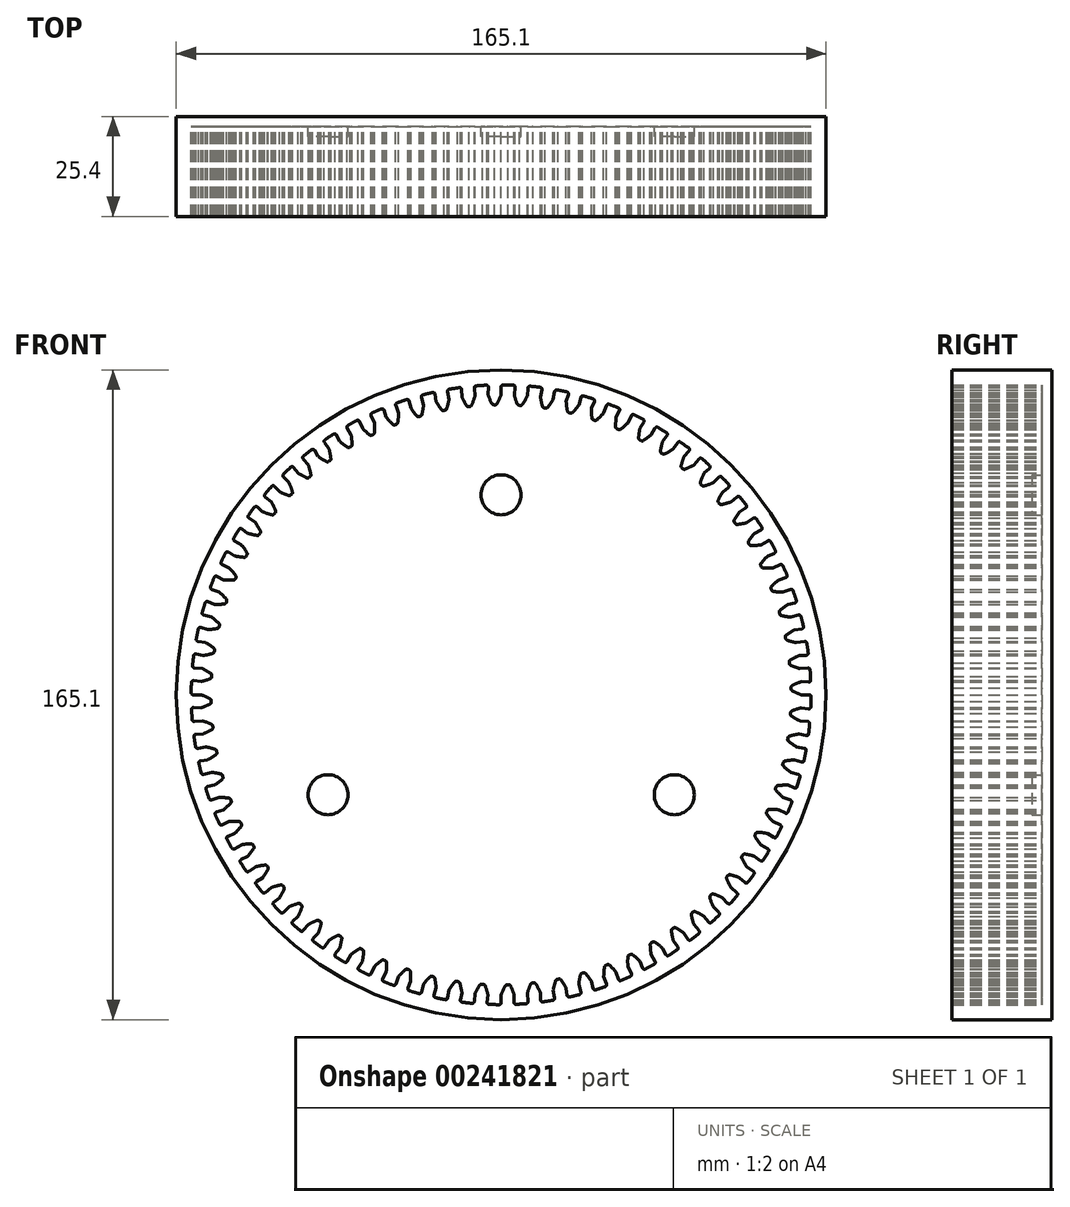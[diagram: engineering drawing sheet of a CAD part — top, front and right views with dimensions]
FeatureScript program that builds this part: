
annotation { "Feature Type Name" : "Feature", "Feature Type Description" : "" }
export const myFeature = defineFeature(function(context is Context, id is Id, definition is map)
    precondition{}
    {
        {
            var Q0;
            Q0=qCreatedBy(makeId("Front.planeOp"),FACE);
            var sketch = newSketch(context, id + "F0", { "sketchPlane" : qUnion([Q0])});
            skArc(sketch, "E0", {"start": v(-3.78, 78.65) * mm, "mid": v(-5.06, 78.58) * mm, "end": v(-6.35, 78.48) * mm});
            skLineSegment(sketch, "E1.MirrorCS", {"start": v(-1.94, 73.68) * mm, "end": v(-1.72, 73.67) * mm});
            skLineSegment(sketch, "E2.MirrorCS", {"start": v(-1.5, 73.67) * mm, "end": v(-1.72, 73.67) * mm});
            skArc(sketch, "E3.MirrorCS", {"start": v(0, 76.2) * mm, "mid": v(-0.49, 75.05) * mm, "end": v(-1.05, 73.93) * mm});
            skArc(sketch, "E4.MirrorCS", {"start": v(-3.32, 76.27) * mm, "mid": v(-2.89, 75.1) * mm, "end": v(-2.38, 73.96) * mm});
            skLineSegment(sketch, "E5.MirrorCS", {"start": v(-3.32, 76.27) * mm, "end": v(-3.24, 78.12) * mm});
            skLineSegment(sketch, "E6.MirrorCS", {"start": v(0, 76.2) * mm, "end": v(0, 78.23) * mm});
            skPoint(sketch, "E7.visualSharp", {"position": v(-1.2, 73.67) * mm});
            skArc(sketch, "E7.filletArc", {"start": v(-1.5, 73.67) * mm, "mid": v(-1.23, 73.74) * mm, "end": v(-1.05, 73.93) * mm});
            skPoint(sketch, "E8.visualSharp", {"position": v(0, 78.74) * mm});
            skArc(sketch, "E8.filletArc", {"start": v(0.51, 78.74) * mm, "mid": v(0.15, 78.6) * mm, "end": v(0, 78.23) * mm});
            skPoint(sketch, "E9.visualSharp", {"position": v(-3.22, 78.67) * mm});
            skArc(sketch, "E9.filletArc", {"start": v(-3.24, 78.12) * mm, "mid": v(-3.4, 78.5) * mm, "end": v(-3.78, 78.65) * mm});
            skPoint(sketch, "E10.visualSharp", {"position": v(-2.24, 73.7) * mm});
            skArc(sketch, "E10.filletArc", {"start": v(-2.38, 73.96) * mm, "mid": v(-2.2, 73.76) * mm, "end": v(-1.94, 73.68) * mm});
            skArc(sketch, "E11.1.0", {"start": v(-6.35, 78.48) * mm, "mid": v(-6.7, 78.3) * mm, "end": v(-6.82, 77.93) * mm});
            skLineSegment(sketch, "E11.1.1", {"start": v(-6.64, 75.91) * mm, "end": v(-6.82, 77.93) * mm});
            skArc(sketch, "E11.1.2", {"start": v(-6.64, 75.91) * mm, "mid": v(-7.03, 74.72) * mm, "end": v(-7.49, 73.56) * mm});
            skArc(sketch, "E11.1.3", {"start": v(-7.9, 73.26) * mm, "mid": v(-7.66, 73.35) * mm, "end": v(-7.49, 73.56) * mm});
            skLineSegment(sketch, "E11.1.4", {"start": v(-7.9, 73.26) * mm, "end": v(-8.13, 73.24) * mm});
            skLineSegment(sketch, "E11.1.5", {"start": v(-8.36, 73.23) * mm, "end": v(-8.13, 73.24) * mm});
            skArc(sketch, "E11.1.6", {"start": v(-8.81, 73.47) * mm, "mid": v(-8.62, 73.29) * mm, "end": v(-8.36, 73.23) * mm});
            skArc(sketch, "E11.1.7", {"start": v(-9.96, 75.7) * mm, "mid": v(-9.42, 74.56) * mm, "end": v(-8.81, 73.47) * mm});
            skLineSegment(sketch, "E11.1.8", {"start": v(-9.96, 75.7) * mm, "end": v(-10.04, 77.54) * mm});
            skArc(sketch, "E11.1.9", {"start": v(-10.04, 77.54) * mm, "mid": v(-10.22, 77.9) * mm, "end": v(-10.62, 78.02) * mm});
            skArc(sketch, "E11.2.0", {"start": v(-13.17, 77.63) * mm, "mid": v(-13.5, 77.42) * mm, "end": v(-13.58, 77.04) * mm});
            skLineSegment(sketch, "E11.2.1", {"start": v(-13.23, 75.04) * mm, "end": v(-13.58, 77.04) * mm});
            skArc(sketch, "E11.2.2", {"start": v(-13.23, 75.04) * mm, "mid": v(-13.51, 73.83) * mm, "end": v(-13.87, 72.63) * mm});
            skArc(sketch, "E11.2.3", {"start": v(-14.26, 72.3) * mm, "mid": v(-14.02, 72.4) * mm, "end": v(-13.87, 72.63) * mm});
            skLineSegment(sketch, "E11.2.4", {"start": v(-14.26, 72.3) * mm, "end": v(-14.48, 72.25) * mm});
            skLineSegment(sketch, "E11.2.5", {"start": v(-14.7, 72.22) * mm, "end": v(-14.48, 72.25) * mm});
            skArc(sketch, "E11.2.6", {"start": v(-15.18, 72.43) * mm, "mid": v(-14.97, 72.26) * mm, "end": v(-14.7, 72.22) * mm});
            skArc(sketch, "E11.2.7", {"start": v(-16.52, 74.54) * mm, "mid": v(-15.89, 73.46) * mm, "end": v(-15.18, 72.43) * mm});
            skLineSegment(sketch, "E11.2.8", {"start": v(-16.52, 74.54) * mm, "end": v(-16.76, 76.37) * mm});
            skArc(sketch, "E11.2.9", {"start": v(-16.76, 76.37) * mm, "mid": v(-16.97, 76.72) * mm, "end": v(-17.37, 76.8) * mm});
            skArc(sketch, "E11.3.0", {"start": v(-19.89, 76.19) * mm, "mid": v(-20.2, 75.95) * mm, "end": v(-20.25, 75.56) * mm});
            skLineSegment(sketch, "E11.3.1", {"start": v(-19.72, 73.6) * mm, "end": v(-20.25, 75.56) * mm});
            skArc(sketch, "E11.3.2", {"start": v(-19.72, 73.6) * mm, "mid": v(-19.9, 72.37) * mm, "end": v(-20.15, 71.14) * mm});
            skArc(sketch, "E11.3.3", {"start": v(-20.5, 70.77) * mm, "mid": v(-20.28, 70.9) * mm, "end": v(-20.15, 71.14) * mm});
            skLineSegment(sketch, "E11.3.4", {"start": v(-20.5, 70.77) * mm, "end": v(-20.73, 70.71) * mm});
            skLineSegment(sketch, "E11.3.5", {"start": v(-20.95, 70.67) * mm, "end": v(-20.73, 70.71) * mm});
            skArc(sketch, "E11.3.6", {"start": v(-21.44, 70.83) * mm, "mid": v(-21.21, 70.68) * mm, "end": v(-20.95, 70.67) * mm});
            skArc(sketch, "E11.3.7", {"start": v(-22.95, 72.81) * mm, "mid": v(-22.23, 71.8) * mm, "end": v(-21.44, 70.83) * mm});
            skLineSegment(sketch, "E11.3.8", {"start": v(-22.95, 72.81) * mm, "end": v(-23.35, 74.62) * mm});
            skArc(sketch, "E11.3.9", {"start": v(-23.35, 74.62) * mm, "mid": v(-23.6, 74.95) * mm, "end": v(-24, 75) * mm});
            skArc(sketch, "E11.4.0", {"start": v(-26.45, 74.16) * mm, "mid": v(-26.74, 73.9) * mm, "end": v(-26.76, 73.51) * mm});
            skLineSegment(sketch, "E11.4.1", {"start": v(-26.06, 71.6) * mm, "end": v(-26.76, 73.51) * mm});
            skArc(sketch, "E11.4.2", {"start": v(-26.06, 71.6) * mm, "mid": v(-26.13, 70.36) * mm, "end": v(-26.27, 69.12) * mm});
            skArc(sketch, "E11.4.3", {"start": v(-26.6, 68.72) * mm, "mid": v(-26.38, 68.87) * mm, "end": v(-26.27, 69.12) * mm});
            skLineSegment(sketch, "E11.4.4", {"start": v(-26.6, 68.72) * mm, "end": v(-26.81, 68.64) * mm});
            skLineSegment(sketch, "E11.4.5", {"start": v(-27.03, 68.57) * mm, "end": v(-26.81, 68.64) * mm});
            skArc(sketch, "E11.4.6", {"start": v(-27.53, 68.69) * mm, "mid": v(-27.3, 68.56) * mm, "end": v(-27.03, 68.57) * mm});
            skArc(sketch, "E11.4.7", {"start": v(-29.21, 70.54) * mm, "mid": v(-28.4, 69.59) * mm, "end": v(-27.53, 68.69) * mm});
            skLineSegment(sketch, "E11.4.8", {"start": v(-29.21, 70.54) * mm, "end": v(-29.77, 72.3) * mm});
            skArc(sketch, "E11.4.9", {"start": v(-29.77, 72.3) * mm, "mid": v(-30.04, 72.6) * mm, "end": v(-30.45, 72.62) * mm});
            skArc(sketch, "E11.5.0", {"start": v(-32.81, 71.58) * mm, "mid": v(-33.08, 71.3) * mm, "end": v(-33.06, 70.9) * mm});
            skLineSegment(sketch, "E11.5.1", {"start": v(-32.2, 69.06) * mm, "end": v(-33.06, 70.9) * mm});
            skArc(sketch, "E11.5.2", {"start": v(-32.2, 69.06) * mm, "mid": v(-32.16, 67.81) * mm, "end": v(-32.2, 66.56) * mm});
            skArc(sketch, "E11.5.3", {"start": v(-32.49, 66.14) * mm, "mid": v(-32.28, 66.31) * mm, "end": v(-32.2, 66.56) * mm});
            skLineSegment(sketch, "E11.5.4", {"start": v(-32.49, 66.14) * mm, "end": v(-32.7, 66.04) * mm});
            skLineSegment(sketch, "E11.5.5", {"start": v(-32.9, 65.95) * mm, "end": v(-32.7, 66.04) * mm});
            skArc(sketch, "E11.5.6", {"start": v(-33.41, 66.03) * mm, "mid": v(-33.17, 65.92) * mm, "end": v(-32.9, 65.95) * mm});
            skArc(sketch, "E11.5.7", {"start": v(-35.25, 67.72) * mm, "mid": v(-34.36, 66.85) * mm, "end": v(-33.41, 66.03) * mm});
            skLineSegment(sketch, "E11.5.8", {"start": v(-35.25, 67.72) * mm, "end": v(-35.95, 69.43) * mm});
            skArc(sketch, "E11.5.9", {"start": v(-35.95, 69.43) * mm, "mid": v(-36.25, 69.71) * mm, "end": v(-36.66, 69.69) * mm});
            skArc(sketch, "E11.6.0", {"start": v(-38.93, 68.45) * mm, "mid": v(-39.17, 68.14) * mm, "end": v(-39.12, 67.75) * mm});
            skLineSegment(sketch, "E11.6.1", {"start": v(-38.1, 66) * mm, "end": v(-39.12, 67.75) * mm});
            skArc(sketch, "E11.6.2", {"start": v(-38.1, 66) * mm, "mid": v(-37.95, 64.75) * mm, "end": v(-37.87, 63.5) * mm});
            skArc(sketch, "E11.6.3", {"start": v(-38.13, 63.05) * mm, "mid": v(-37.94, 63.24) * mm, "end": v(-37.87, 63.5) * mm});
            skLineSegment(sketch, "E11.6.4", {"start": v(-38.13, 63.05) * mm, "end": v(-38.32, 62.94) * mm});
            skLineSegment(sketch, "E11.6.5", {"start": v(-38.52, 62.84) * mm, "end": v(-38.32, 62.94) * mm});
            skArc(sketch, "E11.6.6", {"start": v(-39.04, 62.87) * mm, "mid": v(-38.79, 62.78) * mm, "end": v(-38.52, 62.84) * mm});
            skArc(sketch, "E11.6.7", {"start": v(-41.01, 64.4) * mm, "mid": v(-40.05, 63.6) * mm, "end": v(-39.04, 62.87) * mm});
            skLineSegment(sketch, "E11.6.8", {"start": v(-41.01, 64.4) * mm, "end": v(-41.87, 66.03) * mm});
            skArc(sketch, "E11.6.9", {"start": v(-41.87, 66.03) * mm, "mid": v(-42.19, 66.29) * mm, "end": v(-42.6, 66.22) * mm});
            skArc(sketch, "E11.7.0", {"start": v(-44.74, 64.8) * mm, "mid": v(-44.95, 64.46) * mm, "end": v(-44.87, 64.08) * mm});
            skLineSegment(sketch, "E11.7.1", {"start": v(-43.7, 62.42) * mm, "end": v(-44.87, 64.08) * mm});
            skArc(sketch, "E11.7.2", {"start": v(-43.7, 62.42) * mm, "mid": v(-43.45, 61.2) * mm, "end": v(-43.26, 59.96) * mm});
            skArc(sketch, "E11.7.3", {"start": v(-43.48, 59.49) * mm, "mid": v(-43.3, 59.7) * mm, "end": v(-43.26, 59.96) * mm});
            skLineSegment(sketch, "E11.7.4", {"start": v(-43.48, 59.49) * mm, "end": v(-43.66, 59.36) * mm});
            skLineSegment(sketch, "E11.7.5", {"start": v(-43.85, 59.24) * mm, "end": v(-43.66, 59.36) * mm});
            skArc(sketch, "E11.7.6", {"start": v(-44.37, 59.22) * mm, "mid": v(-44.1, 59.16) * mm, "end": v(-43.85, 59.24) * mm});
            skArc(sketch, "E11.7.7", {"start": v(-46.47, 60.57) * mm, "mid": v(-45.44, 59.86) * mm, "end": v(-44.37, 59.22) * mm});
            skLineSegment(sketch, "E11.7.8", {"start": v(-46.47, 60.57) * mm, "end": v(-47.46, 62.13) * mm});
            skArc(sketch, "E11.7.9", {"start": v(-47.46, 62.13) * mm, "mid": v(-47.8, 62.36) * mm, "end": v(-48.2, 62.26) * mm});
            skArc(sketch, "E11.8.0", {"start": v(-50.22, 60.65) * mm, "mid": v(-50.4, 60.3) * mm, "end": v(-50.29, 59.93) * mm});
            skLineSegment(sketch, "E11.8.1", {"start": v(-48.98, 58.37) * mm, "end": v(-50.29, 59.93) * mm});
            skArc(sketch, "E11.8.2", {"start": v(-48.98, 58.37) * mm, "mid": v(-48.61, 57.18) * mm, "end": v(-48.33, 55.96) * mm});
            skArc(sketch, "E11.8.3", {"start": v(-48.5, 55.47) * mm, "mid": v(-48.34, 55.7) * mm, "end": v(-48.33, 55.96) * mm});
            skLineSegment(sketch, "E11.8.4", {"start": v(-48.5, 55.47) * mm, "end": v(-48.67, 55.33) * mm});
            skLineSegment(sketch, "E11.8.5", {"start": v(-48.85, 55.2) * mm, "end": v(-48.67, 55.33) * mm});
            skArc(sketch, "E11.8.6", {"start": v(-49.36, 55.13) * mm, "mid": v(-49.1, 55.1) * mm, "end": v(-48.85, 55.2) * mm});
            skArc(sketch, "E11.8.7", {"start": v(-51.57, 56.3) * mm, "mid": v(-50.49, 55.68) * mm, "end": v(-49.36, 55.13) * mm});
            skLineSegment(sketch, "E11.8.8", {"start": v(-51.57, 56.3) * mm, "end": v(-52.7, 57.76) * mm});
            skArc(sketch, "E11.8.9", {"start": v(-52.7, 57.76) * mm, "mid": v(-53.06, 57.96) * mm, "end": v(-53.45, 57.82) * mm});
            skArc(sketch, "E11.9.0", {"start": v(-55.31, 56.04) * mm, "mid": v(-55.47, 55.68) * mm, "end": v(-55.32, 55.32) * mm});
            skLineSegment(sketch, "E11.9.1", {"start": v(-53.88, 53.88) * mm, "end": v(-55.32, 55.32) * mm});
            skArc(sketch, "E11.9.2", {"start": v(-53.88, 53.88) * mm, "mid": v(-53.41, 52.72) * mm, "end": v(-53.02, 51.54) * mm});
            skArc(sketch, "E11.9.3", {"start": v(-53.15, 51.04) * mm, "mid": v(-53.01, 51.27) * mm, "end": v(-53.02, 51.54) * mm});
            skLineSegment(sketch, "E11.9.4", {"start": v(-53.15, 51.04) * mm, "end": v(-53.3, 50.88) * mm});
            skLineSegment(sketch, "E11.9.5", {"start": v(-53.47, 50.73) * mm, "end": v(-53.3, 50.88) * mm});
            skArc(sketch, "E11.9.6", {"start": v(-53.98, 50.62) * mm, "mid": v(-53.71, 50.6) * mm, "end": v(-53.47, 50.73) * mm});
            skArc(sketch, "E11.9.7", {"start": v(-56.28, 51.58) * mm, "mid": v(-55.15, 51.06) * mm, "end": v(-53.98, 50.62) * mm});
            skLineSegment(sketch, "E11.9.8", {"start": v(-56.28, 51.58) * mm, "end": v(-57.53, 52.95) * mm});
            skArc(sketch, "E11.9.9", {"start": v(-57.53, 52.95) * mm, "mid": v(-57.9, 53.11) * mm, "end": v(-58.28, 52.94) * mm});
            skArc(sketch, "E11.10.0", {"start": v(-59.99, 51) * mm, "mid": v(-60.1, 50.63) * mm, "end": v(-59.93, 50.29) * mm});
            skLineSegment(sketch, "E11.10.1", {"start": v(-58.37, 48.98) * mm, "end": v(-59.93, 50.29) * mm});
            skArc(sketch, "E11.10.2", {"start": v(-58.37, 48.98) * mm, "mid": v(-57.8, 47.87) * mm, "end": v(-57.3, 46.72) * mm});
            skArc(sketch, "E11.10.3", {"start": v(-57.4, 46.21) * mm, "mid": v(-57.28, 46.45) * mm, "end": v(-57.3, 46.72) * mm});
            skLineSegment(sketch, "E11.10.4", {"start": v(-57.4, 46.21) * mm, "end": v(-57.54, 46.04) * mm});
            skLineSegment(sketch, "E11.10.5", {"start": v(-57.7, 45.87) * mm, "end": v(-57.54, 46.04) * mm});
            skArc(sketch, "E11.10.6", {"start": v(-58.19, 45.72) * mm, "mid": v(-57.92, 45.73) * mm, "end": v(-57.7, 45.87) * mm});
            skArc(sketch, "E11.10.7", {"start": v(-60.56, 46.48) * mm, "mid": v(-59.39, 46.06) * mm, "end": v(-58.19, 45.72) * mm});
            skLineSegment(sketch, "E11.10.8", {"start": v(-60.56, 46.48) * mm, "end": v(-61.93, 47.73) * mm});
            skArc(sketch, "E11.10.9", {"start": v(-61.93, 47.73) * mm, "mid": v(-62.32, 47.86) * mm, "end": v(-62.68, 47.66) * mm});
            skArc(sketch, "E11.11.0", {"start": v(-64.2, 45.58) * mm, "mid": v(-64.3, 45.2) * mm, "end": v(-64.08, 44.87) * mm});
            skLineSegment(sketch, "E11.11.1", {"start": v(-62.42, 43.7) * mm, "end": v(-64.08, 44.87) * mm});
            skArc(sketch, "E11.11.2", {"start": v(-62.42, 43.7) * mm, "mid": v(-61.76, 42.65) * mm, "end": v(-61.16, 41.55) * mm});
            skArc(sketch, "E11.11.3", {"start": v(-61.2, 41.03) * mm, "mid": v(-61.11, 41.29) * mm, "end": v(-61.16, 41.55) * mm});
            skLineSegment(sketch, "E11.11.4", {"start": v(-61.2, 41.03) * mm, "end": v(-61.33, 40.85) * mm});
            skLineSegment(sketch, "E11.11.5", {"start": v(-61.47, 40.67) * mm, "end": v(-61.33, 40.85) * mm});
            skArc(sketch, "E11.11.6", {"start": v(-61.95, 40.48) * mm, "mid": v(-61.68, 40.5) * mm, "end": v(-61.47, 40.67) * mm});
            skArc(sketch, "E11.11.7", {"start": v(-64.39, 41.03) * mm, "mid": v(-63.18, 40.71) * mm, "end": v(-61.95, 40.48) * mm});
            skLineSegment(sketch, "E11.11.8", {"start": v(-64.39, 41.03) * mm, "end": v(-65.85, 42.15) * mm});
            skArc(sketch, "E11.11.9", {"start": v(-65.85, 42.15) * mm, "mid": v(-66.25, 42.25) * mm, "end": v(-66.6, 42.02) * mm});
            skArc(sketch, "E11.12.0", {"start": v(-67.93, 39.81) * mm, "mid": v(-67.99, 39.43) * mm, "end": v(-67.75, 39.12) * mm});
            skLineSegment(sketch, "E11.12.1", {"start": v(-66, 38.1) * mm, "end": v(-67.75, 39.12) * mm});
            skArc(sketch, "E11.12.2", {"start": v(-66, 38.1) * mm, "mid": v(-65.24, 37.1) * mm, "end": v(-64.55, 36.06) * mm});
            skArc(sketch, "E11.12.3", {"start": v(-64.55, 35.54) * mm, "mid": v(-64.48, 35.8) * mm, "end": v(-64.55, 36.06) * mm});
            skLineSegment(sketch, "E11.12.4", {"start": v(-64.55, 35.54) * mm, "end": v(-64.66, 35.35) * mm});
            skLineSegment(sketch, "E11.12.5", {"start": v(-64.78, 35.16) * mm, "end": v(-64.66, 35.35) * mm});
            skArc(sketch, "E11.12.6", {"start": v(-65.24, 34.92) * mm, "mid": v(-64.98, 34.98) * mm, "end": v(-64.78, 35.16) * mm});
            skArc(sketch, "E11.12.7", {"start": v(-67.72, 35.26) * mm, "mid": v(-66.48, 35.05) * mm, "end": v(-65.24, 34.92) * mm});
            skLineSegment(sketch, "E11.12.8", {"start": v(-67.72, 35.26) * mm, "end": v(-69.28, 36.25) * mm});
            skArc(sketch, "E11.12.9", {"start": v(-69.28, 36.25) * mm, "mid": v(-69.68, 36.31) * mm, "end": v(-70, 36.06) * mm});
            skArc(sketch, "E11.13.0", {"start": v(-71.15, 33.74) * mm, "mid": v(-71.16, 33.35) * mm, "end": v(-70.9, 33.06) * mm});
            skLineSegment(sketch, "E11.13.1", {"start": v(-69.06, 32.2) * mm, "end": v(-70.9, 33.06) * mm});
            skArc(sketch, "E11.13.2", {"start": v(-69.06, 32.2) * mm, "mid": v(-68.22, 31.28) * mm, "end": v(-67.45, 30.3) * mm});
            skArc(sketch, "E11.13.3", {"start": v(-67.4, 29.78) * mm, "mid": v(-67.35, 30.05) * mm, "end": v(-67.45, 30.3) * mm});
            skLineSegment(sketch, "E11.13.4", {"start": v(-67.4, 29.78) * mm, "end": v(-67.5, 29.58) * mm});
            skLineSegment(sketch, "E11.13.5", {"start": v(-67.6, 29.38) * mm, "end": v(-67.5, 29.58) * mm});
            skArc(sketch, "E11.13.6", {"start": v(-68.04, 29.1) * mm, "mid": v(-67.78, 29.18) * mm, "end": v(-67.6, 29.38) * mm});
            skArc(sketch, "E11.13.7", {"start": v(-70.53, 29.22) * mm, "mid": v(-69.29, 29.12) * mm, "end": v(-68.04, 29.1) * mm});
            skLineSegment(sketch, "E11.13.8", {"start": v(-70.53, 29.22) * mm, "end": v(-72.17, 30.08) * mm});
            skArc(sketch, "E11.13.9", {"start": v(-72.17, 30.08) * mm, "mid": v(-72.58, 30.1) * mm, "end": v(-72.88, 29.82) * mm});
            skArc(sketch, "E11.14.0", {"start": v(-73.81, 27.41) * mm, "mid": v(-73.8, 27.02) * mm, "end": v(-73.51, 26.76) * mm});
            skLineSegment(sketch, "E11.14.1", {"start": v(-71.6, 26.06) * mm, "end": v(-73.51, 26.76) * mm});
            skArc(sketch, "E11.14.2", {"start": v(-71.6, 26.06) * mm, "mid": v(-70.7, 25.21) * mm, "end": v(-69.83, 24.3) * mm});
            skArc(sketch, "E11.14.3", {"start": v(-69.74, 23.8) * mm, "mid": v(-69.72, 24.06) * mm, "end": v(-69.83, 24.3) * mm});
            skLineSegment(sketch, "E11.14.4", {"start": v(-69.74, 23.8) * mm, "end": v(-69.81, 23.58) * mm});
            skLineSegment(sketch, "E11.14.5", {"start": v(-69.9, 23.37) * mm, "end": v(-69.81, 23.58) * mm});
            skArc(sketch, "E11.14.6", {"start": v(-70.32, 23.06) * mm, "mid": v(-70.07, 23.16) * mm, "end": v(-69.9, 23.37) * mm});
            skArc(sketch, "E11.14.7", {"start": v(-72.8, 22.96) * mm, "mid": v(-71.56, 22.97) * mm, "end": v(-70.32, 23.06) * mm});
            skLineSegment(sketch, "E11.14.8", {"start": v(-72.8, 22.96) * mm, "end": v(-74.52, 23.67) * mm});
            skArc(sketch, "E11.14.9", {"start": v(-74.52, 23.67) * mm, "mid": v(-74.93, 23.66) * mm, "end": v(-75.2, 23.35) * mm});
            skArc(sketch, "E11.15.0", {"start": v(-75.92, 20.87) * mm, "mid": v(-75.87, 20.49) * mm, "end": v(-75.56, 20.25) * mm});
            skLineSegment(sketch, "E11.15.1", {"start": v(-73.6, 19.72) * mm, "end": v(-75.56, 20.25) * mm});
            skArc(sketch, "E11.15.2", {"start": v(-73.6, 19.72) * mm, "mid": v(-72.62, 18.95) * mm, "end": v(-71.69, 18.12) * mm});
            skArc(sketch, "E11.15.3", {"start": v(-71.55, 17.63) * mm, "mid": v(-71.55, 17.9) * mm, "end": v(-71.69, 18.12) * mm});
            skLineSegment(sketch, "E11.15.4", {"start": v(-71.55, 17.63) * mm, "end": v(-71.6, 17.4) * mm});
            skLineSegment(sketch, "E11.15.5", {"start": v(-71.67, 17.2) * mm, "end": v(-71.6, 17.4) * mm});
            skArc(sketch, "E11.15.6", {"start": v(-72.06, 16.85) * mm, "mid": v(-71.82, 16.97) * mm, "end": v(-71.67, 17.2) * mm});
            skArc(sketch, "E11.15.7", {"start": v(-74.53, 16.53) * mm, "mid": v(-73.3, 16.65) * mm, "end": v(-72.06, 16.85) * mm});
            skLineSegment(sketch, "E11.15.8", {"start": v(-74.53, 16.53) * mm, "end": v(-76.3, 17.09) * mm});
            skArc(sketch, "E11.15.9", {"start": v(-76.3, 17.09) * mm, "mid": v(-76.7, 17.04) * mm, "end": v(-76.95, 16.7) * mm});
            skArc(sketch, "E11.16.0", {"start": v(-77.45, 14.18) * mm, "mid": v(-77.37, 13.8) * mm, "end": v(-77.04, 13.58) * mm});
            skLineSegment(sketch, "E11.16.1", {"start": v(-75.04, 13.23) * mm, "end": v(-77.04, 13.58) * mm});
            skArc(sketch, "E11.16.2", {"start": v(-75.04, 13.23) * mm, "mid": v(-74, 12.55) * mm, "end": v(-73, 11.8) * mm});
            skArc(sketch, "E11.16.3", {"start": v(-72.8, 11.32) * mm, "mid": v(-72.83, 11.6) * mm, "end": v(-73, 11.8) * mm});
            skLineSegment(sketch, "E11.16.4", {"start": v(-72.8, 11.32) * mm, "end": v(-72.85, 11.1) * mm});
            skLineSegment(sketch, "E11.16.5", {"start": v(-72.9, 10.88) * mm, "end": v(-72.85, 11.1) * mm});
            skArc(sketch, "E11.16.6", {"start": v(-73.25, 10.5) * mm, "mid": v(-73.02, 10.64) * mm, "end": v(-72.9, 10.88) * mm});
            skArc(sketch, "E11.16.7", {"start": v(-75.7, 9.97) * mm, "mid": v(-74.46, 10.2) * mm, "end": v(-73.25, 10.5) * mm});
            skLineSegment(sketch, "E11.16.8", {"start": v(-75.7, 9.97) * mm, "end": v(-77.5, 10.37) * mm});
            skArc(sketch, "E11.16.9", {"start": v(-77.5, 10.37) * mm, "mid": v(-77.9, 10.3) * mm, "end": v(-78.11, 9.94) * mm});
            skArc(sketch, "E11.17.0", {"start": v(-78.4, 7.37) * mm, "mid": v(-78.28, 7) * mm, "end": v(-77.93, 6.82) * mm});
            skLineSegment(sketch, "E11.17.1", {"start": v(-75.91, 6.64) * mm, "end": v(-77.93, 6.82) * mm});
            skArc(sketch, "E11.17.2", {"start": v(-75.91, 6.64) * mm, "mid": v(-74.8, 6.06) * mm, "end": v(-73.74, 5.4) * mm});
            skArc(sketch, "E11.17.3", {"start": v(-73.52, 4.93) * mm, "mid": v(-73.57, 5.2) * mm, "end": v(-73.74, 5.4) * mm});
            skLineSegment(sketch, "E11.17.4", {"start": v(-73.52, 4.93) * mm, "end": v(-73.54, 4.7) * mm});
            skLineSegment(sketch, "E11.17.5", {"start": v(-73.57, 4.49) * mm, "end": v(-73.54, 4.7) * mm});
            skArc(sketch, "E11.17.6", {"start": v(-73.89, 4.08) * mm, "mid": v(-73.67, 4.24) * mm, "end": v(-73.57, 4.49) * mm});
            skArc(sketch, "E11.17.7", {"start": v(-76.27, 3.34) * mm, "mid": v(-75.07, 3.67) * mm, "end": v(-73.89, 4.08) * mm});
            skLineSegment(sketch, "E11.17.8", {"start": v(-76.27, 3.34) * mm, "end": v(-78.1, 3.58) * mm});
            skArc(sketch, "E11.17.9", {"start": v(-78.1, 3.58) * mm, "mid": v(-78.5, 3.46) * mm, "end": v(-78.68, 3.1) * mm});
            skArc(sketch, "E11.18.0", {"start": v(-78.74, 0.51) * mm, "mid": v(-78.6, 0.15) * mm, "end": v(-78.23, 0) * mm});
            skLineSegment(sketch, "E11.18.1", {"start": v(-76.2, 0) * mm, "end": v(-78.23, 0) * mm});
            skArc(sketch, "E11.18.2", {"start": v(-76.2, 0) * mm, "mid": v(-75.05, -0.49) * mm, "end": v(-73.93, -1.05) * mm});
            skArc(sketch, "E11.18.3", {"start": v(-73.67, -1.5) * mm, "mid": v(-73.74, -1.23) * mm, "end": v(-73.93, -1.05) * mm});
            skLineSegment(sketch, "E11.18.4", {"start": v(-73.67, -1.5) * mm, "end": v(-73.67, -1.72) * mm});
            skLineSegment(sketch, "E11.18.5", {"start": v(-73.68, -1.94) * mm, "end": v(-73.67, -1.72) * mm});
            skArc(sketch, "E11.18.6", {"start": v(-73.96, -2.38) * mm, "mid": v(-73.76, -2.2) * mm, "end": v(-73.68, -1.94) * mm});
            skArc(sketch, "E11.18.7", {"start": v(-76.27, -3.32) * mm, "mid": v(-75.1, -2.89) * mm, "end": v(-73.96, -2.38) * mm});
            skLineSegment(sketch, "E11.18.8", {"start": v(-76.27, -3.32) * mm, "end": v(-78.12, -3.24) * mm});
            skArc(sketch, "E11.18.9", {"start": v(-78.12, -3.24) * mm, "mid": v(-78.5, -3.4) * mm, "end": v(-78.65, -3.78) * mm});
            skArc(sketch, "E11.19.0", {"start": v(-78.48, -6.35) * mm, "mid": v(-78.3, -6.7) * mm, "end": v(-77.93, -6.82) * mm});
            skLineSegment(sketch, "E11.19.1", {"start": v(-75.91, -6.64) * mm, "end": v(-77.93, -6.82) * mm});
            skArc(sketch, "E11.19.2", {"start": v(-75.91, -6.64) * mm, "mid": v(-74.72, -7.03) * mm, "end": v(-73.56, -7.49) * mm});
            skArc(sketch, "E11.19.3", {"start": v(-73.26, -7.9) * mm, "mid": v(-73.35, -7.66) * mm, "end": v(-73.56, -7.49) * mm});
            skLineSegment(sketch, "E11.19.4", {"start": v(-73.26, -7.9) * mm, "end": v(-73.24, -8.13) * mm});
            skLineSegment(sketch, "E11.19.5", {"start": v(-73.23, -8.36) * mm, "end": v(-73.24, -8.13) * mm});
            skArc(sketch, "E11.19.6", {"start": v(-73.47, -8.81) * mm, "mid": v(-73.29, -8.62) * mm, "end": v(-73.23, -8.36) * mm});
            skArc(sketch, "E11.19.7", {"start": v(-75.7, -9.96) * mm, "mid": v(-74.56, -9.42) * mm, "end": v(-73.47, -8.81) * mm});
            skLineSegment(sketch, "E11.19.8", {"start": v(-75.7, -9.96) * mm, "end": v(-77.54, -10.04) * mm});
            skArc(sketch, "E11.19.9", {"start": v(-77.54, -10.04) * mm, "mid": v(-77.9, -10.22) * mm, "end": v(-78.02, -10.62) * mm});
            skArc(sketch, "E11.20.0", {"start": v(-77.63, -13.17) * mm, "mid": v(-77.42, -13.5) * mm, "end": v(-77.04, -13.58) * mm});
            skLineSegment(sketch, "E11.20.1", {"start": v(-75.04, -13.23) * mm, "end": v(-77.04, -13.58) * mm});
            skArc(sketch, "E11.20.2", {"start": v(-75.04, -13.23) * mm, "mid": v(-73.83, -13.51) * mm, "end": v(-72.63, -13.87) * mm});
            skArc(sketch, "E11.20.3", {"start": v(-72.3, -14.26) * mm, "mid": v(-72.4, -14.02) * mm, "end": v(-72.63, -13.87) * mm});
            skLineSegment(sketch, "E11.20.4", {"start": v(-72.3, -14.26) * mm, "end": v(-72.25, -14.48) * mm});
            skLineSegment(sketch, "E11.20.5", {"start": v(-72.22, -14.7) * mm, "end": v(-72.25, -14.48) * mm});
            skArc(sketch, "E11.20.6", {"start": v(-72.43, -15.18) * mm, "mid": v(-72.26, -14.97) * mm, "end": v(-72.22, -14.7) * mm});
            skArc(sketch, "E11.20.7", {"start": v(-74.54, -16.52) * mm, "mid": v(-73.46, -15.89) * mm, "end": v(-72.43, -15.18) * mm});
            skLineSegment(sketch, "E11.20.8", {"start": v(-74.54, -16.52) * mm, "end": v(-76.37, -16.76) * mm});
            skArc(sketch, "E11.20.9", {"start": v(-76.37, -16.76) * mm, "mid": v(-76.72, -16.97) * mm, "end": v(-76.8, -17.37) * mm});
            skArc(sketch, "E11.21.0", {"start": v(-76.19, -19.89) * mm, "mid": v(-75.95, -20.2) * mm, "end": v(-75.56, -20.25) * mm});
            skLineSegment(sketch, "E11.21.1", {"start": v(-73.6, -19.72) * mm, "end": v(-75.56, -20.25) * mm});
            skArc(sketch, "E11.21.2", {"start": v(-73.6, -19.72) * mm, "mid": v(-72.37, -19.9) * mm, "end": v(-71.14, -20.15) * mm});
            skArc(sketch, "E11.21.3", {"start": v(-70.77, -20.5) * mm, "mid": v(-70.9, -20.28) * mm, "end": v(-71.14, -20.15) * mm});
            skLineSegment(sketch, "E11.21.4", {"start": v(-70.77, -20.5) * mm, "end": v(-70.71, -20.73) * mm});
            skLineSegment(sketch, "E11.21.5", {"start": v(-70.67, -20.95) * mm, "end": v(-70.71, -20.73) * mm});
            skArc(sketch, "E11.21.6", {"start": v(-70.83, -21.44) * mm, "mid": v(-70.68, -21.21) * mm, "end": v(-70.67, -20.95) * mm});
            skArc(sketch, "E11.21.7", {"start": v(-72.81, -22.95) * mm, "mid": v(-71.8, -22.23) * mm, "end": v(-70.83, -21.44) * mm});
            skLineSegment(sketch, "E11.21.8", {"start": v(-72.81, -22.95) * mm, "end": v(-74.62, -23.35) * mm});
            skArc(sketch, "E11.21.9", {"start": v(-74.62, -23.35) * mm, "mid": v(-74.95, -23.6) * mm, "end": v(-75, -24) * mm});
            skArc(sketch, "E11.22.0", {"start": v(-74.16, -26.45) * mm, "mid": v(-73.9, -26.74) * mm, "end": v(-73.51, -26.76) * mm});
            skLineSegment(sketch, "E11.22.1", {"start": v(-71.6, -26.06) * mm, "end": v(-73.51, -26.76) * mm});
            skArc(sketch, "E11.22.2", {"start": v(-71.6, -26.06) * mm, "mid": v(-70.36, -26.13) * mm, "end": v(-69.12, -26.27) * mm});
            skArc(sketch, "E11.22.3", {"start": v(-68.72, -26.6) * mm, "mid": v(-68.87, -26.38) * mm, "end": v(-69.12, -26.27) * mm});
            skLineSegment(sketch, "E11.22.4", {"start": v(-68.72, -26.6) * mm, "end": v(-68.64, -26.81) * mm});
            skLineSegment(sketch, "E11.22.5", {"start": v(-68.57, -27.03) * mm, "end": v(-68.64, -26.81) * mm});
            skArc(sketch, "E11.22.6", {"start": v(-68.69, -27.53) * mm, "mid": v(-68.56, -27.3) * mm, "end": v(-68.57, -27.03) * mm});
            skArc(sketch, "E11.22.7", {"start": v(-70.54, -29.21) * mm, "mid": v(-69.59, -28.4) * mm, "end": v(-68.69, -27.53) * mm});
            skLineSegment(sketch, "E11.22.8", {"start": v(-70.54, -29.21) * mm, "end": v(-72.3, -29.77) * mm});
            skArc(sketch, "E11.22.9", {"start": v(-72.3, -29.77) * mm, "mid": v(-72.6, -30.04) * mm, "end": v(-72.62, -30.45) * mm});
            skArc(sketch, "E11.23.0", {"start": v(-71.58, -32.81) * mm, "mid": v(-71.3, -33.08) * mm, "end": v(-70.9, -33.06) * mm});
            skLineSegment(sketch, "E11.23.1", {"start": v(-69.06, -32.2) * mm, "end": v(-70.9, -33.06) * mm});
            skArc(sketch, "E11.23.2", {"start": v(-69.06, -32.2) * mm, "mid": v(-67.81, -32.16) * mm, "end": v(-66.56, -32.2) * mm});
            skArc(sketch, "E11.23.3", {"start": v(-66.14, -32.49) * mm, "mid": v(-66.31, -32.28) * mm, "end": v(-66.56, -32.2) * mm});
            skLineSegment(sketch, "E11.23.4", {"start": v(-66.14, -32.49) * mm, "end": v(-66.04, -32.7) * mm});
            skLineSegment(sketch, "E11.23.5", {"start": v(-65.95, -32.9) * mm, "end": v(-66.04, -32.7) * mm});
            skArc(sketch, "E11.23.6", {"start": v(-66.03, -33.41) * mm, "mid": v(-65.92, -33.17) * mm, "end": v(-65.95, -32.9) * mm});
            skArc(sketch, "E11.23.7", {"start": v(-67.72, -35.25) * mm, "mid": v(-66.85, -34.36) * mm, "end": v(-66.03, -33.41) * mm});
            skLineSegment(sketch, "E11.23.8", {"start": v(-67.72, -35.25) * mm, "end": v(-69.43, -35.95) * mm});
            skArc(sketch, "E11.23.9", {"start": v(-69.43, -35.95) * mm, "mid": v(-69.71, -36.25) * mm, "end": v(-69.69, -36.66) * mm});
            skArc(sketch, "E11.24.0", {"start": v(-68.45, -38.93) * mm, "mid": v(-68.14, -39.17) * mm, "end": v(-67.75, -39.12) * mm});
            skLineSegment(sketch, "E11.24.1", {"start": v(-66, -38.1) * mm, "end": v(-67.75, -39.12) * mm});
            skArc(sketch, "E11.24.2", {"start": v(-66, -38.1) * mm, "mid": v(-64.75, -37.95) * mm, "end": v(-63.5, -37.87) * mm});
            skArc(sketch, "E11.24.3", {"start": v(-63.05, -38.13) * mm, "mid": v(-63.24, -37.94) * mm, "end": v(-63.5, -37.87) * mm});
            skLineSegment(sketch, "E11.24.4", {"start": v(-63.05, -38.13) * mm, "end": v(-62.94, -38.32) * mm});
            skLineSegment(sketch, "E11.24.5", {"start": v(-62.84, -38.52) * mm, "end": v(-62.94, -38.32) * mm});
            skArc(sketch, "E11.24.6", {"start": v(-62.87, -39.04) * mm, "mid": v(-62.78, -38.79) * mm, "end": v(-62.84, -38.52) * mm});
            skArc(sketch, "E11.24.7", {"start": v(-64.4, -41.01) * mm, "mid": v(-63.6, -40.05) * mm, "end": v(-62.87, -39.04) * mm});
            skLineSegment(sketch, "E11.24.8", {"start": v(-64.4, -41.01) * mm, "end": v(-66.03, -41.87) * mm});
            skArc(sketch, "E11.24.9", {"start": v(-66.03, -41.87) * mm, "mid": v(-66.29, -42.19) * mm, "end": v(-66.22, -42.6) * mm});
            skArc(sketch, "E11.25.0", {"start": v(-64.8, -44.74) * mm, "mid": v(-64.46, -44.95) * mm, "end": v(-64.08, -44.87) * mm});
            skLineSegment(sketch, "E11.25.1", {"start": v(-62.42, -43.7) * mm, "end": v(-64.08, -44.87) * mm});
            skArc(sketch, "E11.25.2", {"start": v(-62.42, -43.7) * mm, "mid": v(-61.2, -43.45) * mm, "end": v(-59.96, -43.26) * mm});
            skArc(sketch, "E11.25.3", {"start": v(-59.49, -43.48) * mm, "mid": v(-59.7, -43.3) * mm, "end": v(-59.96, -43.26) * mm});
            skLineSegment(sketch, "E11.25.4", {"start": v(-59.49, -43.48) * mm, "end": v(-59.36, -43.66) * mm});
            skLineSegment(sketch, "E11.25.5", {"start": v(-59.24, -43.85) * mm, "end": v(-59.36, -43.66) * mm});
            skArc(sketch, "E11.25.6", {"start": v(-59.22, -44.37) * mm, "mid": v(-59.16, -44.1) * mm, "end": v(-59.24, -43.85) * mm});
            skArc(sketch, "E11.25.7", {"start": v(-60.57, -46.47) * mm, "mid": v(-59.86, -45.44) * mm, "end": v(-59.22, -44.37) * mm});
            skLineSegment(sketch, "E11.25.8", {"start": v(-60.57, -46.47) * mm, "end": v(-62.13, -47.46) * mm});
            skArc(sketch, "E11.25.9", {"start": v(-62.13, -47.46) * mm, "mid": v(-62.36, -47.8) * mm, "end": v(-62.26, -48.2) * mm});
            skArc(sketch, "E11.26.0", {"start": v(-60.65, -50.22) * mm, "mid": v(-60.3, -50.4) * mm, "end": v(-59.93, -50.29) * mm});
            skLineSegment(sketch, "E11.26.1", {"start": v(-58.37, -48.98) * mm, "end": v(-59.93, -50.29) * mm});
            skArc(sketch, "E11.26.2", {"start": v(-58.37, -48.98) * mm, "mid": v(-57.18, -48.61) * mm, "end": v(-55.96, -48.33) * mm});
            skArc(sketch, "E11.26.3", {"start": v(-55.47, -48.5) * mm, "mid": v(-55.7, -48.34) * mm, "end": v(-55.96, -48.33) * mm});
            skLineSegment(sketch, "E11.26.4", {"start": v(-55.47, -48.5) * mm, "end": v(-55.33, -48.67) * mm});
            skLineSegment(sketch, "E11.26.5", {"start": v(-55.2, -48.85) * mm, "end": v(-55.33, -48.67) * mm});
            skArc(sketch, "E11.26.6", {"start": v(-55.13, -49.36) * mm, "mid": v(-55.1, -49.1) * mm, "end": v(-55.2, -48.85) * mm});
            skArc(sketch, "E11.26.7", {"start": v(-56.3, -51.57) * mm, "mid": v(-55.68, -50.49) * mm, "end": v(-55.13, -49.36) * mm});
            skLineSegment(sketch, "E11.26.8", {"start": v(-56.3, -51.57) * mm, "end": v(-57.76, -52.7) * mm});
            skArc(sketch, "E11.26.9", {"start": v(-57.76, -52.7) * mm, "mid": v(-57.96, -53.06) * mm, "end": v(-57.82, -53.45) * mm});
            skArc(sketch, "E11.27.0", {"start": v(-56.04, -55.31) * mm, "mid": v(-55.68, -55.47) * mm, "end": v(-55.32, -55.32) * mm});
            skLineSegment(sketch, "E11.27.1", {"start": v(-53.88, -53.88) * mm, "end": v(-55.32, -55.32) * mm});
            skArc(sketch, "E11.27.2", {"start": v(-53.88, -53.88) * mm, "mid": v(-52.72, -53.41) * mm, "end": v(-51.54, -53.02) * mm});
            skArc(sketch, "E11.27.3", {"start": v(-51.04, -53.15) * mm, "mid": v(-51.27, -53.01) * mm, "end": v(-51.54, -53.02) * mm});
            skLineSegment(sketch, "E11.27.4", {"start": v(-51.04, -53.15) * mm, "end": v(-50.88, -53.3) * mm});
            skLineSegment(sketch, "E11.27.5", {"start": v(-50.73, -53.47) * mm, "end": v(-50.88, -53.3) * mm});
            skArc(sketch, "E11.27.6", {"start": v(-50.62, -53.98) * mm, "mid": v(-50.6, -53.71) * mm, "end": v(-50.73, -53.47) * mm});
            skArc(sketch, "E11.27.7", {"start": v(-51.58, -56.28) * mm, "mid": v(-51.06, -55.15) * mm, "end": v(-50.62, -53.98) * mm});
            skLineSegment(sketch, "E11.27.8", {"start": v(-51.58, -56.28) * mm, "end": v(-52.95, -57.53) * mm});
            skArc(sketch, "E11.27.9", {"start": v(-52.95, -57.53) * mm, "mid": v(-53.11, -57.9) * mm, "end": v(-52.94, -58.28) * mm});
            skArc(sketch, "E11.28.0", {"start": v(-51, -59.99) * mm, "mid": v(-50.63, -60.1) * mm, "end": v(-50.29, -59.93) * mm});
            skLineSegment(sketch, "E11.28.1", {"start": v(-48.98, -58.37) * mm, "end": v(-50.29, -59.93) * mm});
            skArc(sketch, "E11.28.2", {"start": v(-48.98, -58.37) * mm, "mid": v(-47.87, -57.8) * mm, "end": v(-46.72, -57.3) * mm});
            skArc(sketch, "E11.28.3", {"start": v(-46.21, -57.4) * mm, "mid": v(-46.45, -57.28) * mm, "end": v(-46.72, -57.3) * mm});
            skLineSegment(sketch, "E11.28.4", {"start": v(-46.21, -57.4) * mm, "end": v(-46.04, -57.54) * mm});
            skLineSegment(sketch, "E11.28.5", {"start": v(-45.87, -57.7) * mm, "end": v(-46.04, -57.54) * mm});
            skArc(sketch, "E11.28.6", {"start": v(-45.72, -58.19) * mm, "mid": v(-45.73, -57.92) * mm, "end": v(-45.87, -57.7) * mm});
            skArc(sketch, "E11.28.7", {"start": v(-46.48, -60.56) * mm, "mid": v(-46.06, -59.39) * mm, "end": v(-45.72, -58.19) * mm});
            skLineSegment(sketch, "E11.28.8", {"start": v(-46.48, -60.56) * mm, "end": v(-47.73, -61.93) * mm});
            skArc(sketch, "E11.28.9", {"start": v(-47.73, -61.93) * mm, "mid": v(-47.86, -62.32) * mm, "end": v(-47.66, -62.68) * mm});
            skArc(sketch, "E11.29.0", {"start": v(-45.58, -64.2) * mm, "mid": v(-45.2, -64.3) * mm, "end": v(-44.87, -64.08) * mm});
            skLineSegment(sketch, "E11.29.1", {"start": v(-43.7, -62.42) * mm, "end": v(-44.87, -64.08) * mm});
            skArc(sketch, "E11.29.2", {"start": v(-43.7, -62.42) * mm, "mid": v(-42.65, -61.76) * mm, "end": v(-41.55, -61.16) * mm});
            skArc(sketch, "E11.29.3", {"start": v(-41.03, -61.2) * mm, "mid": v(-41.29, -61.11) * mm, "end": v(-41.55, -61.16) * mm});
            skLineSegment(sketch, "E11.29.4", {"start": v(-41.03, -61.2) * mm, "end": v(-40.85, -61.33) * mm});
            skLineSegment(sketch, "E11.29.5", {"start": v(-40.67, -61.47) * mm, "end": v(-40.85, -61.33) * mm});
            skArc(sketch, "E11.29.6", {"start": v(-40.48, -61.95) * mm, "mid": v(-40.5, -61.68) * mm, "end": v(-40.67, -61.47) * mm});
            skArc(sketch, "E11.29.7", {"start": v(-41.03, -64.39) * mm, "mid": v(-40.71, -63.18) * mm, "end": v(-40.48, -61.95) * mm});
            skLineSegment(sketch, "E11.29.8", {"start": v(-41.03, -64.39) * mm, "end": v(-42.15, -65.85) * mm});
            skArc(sketch, "E11.29.9", {"start": v(-42.15, -65.85) * mm, "mid": v(-42.25, -66.25) * mm, "end": v(-42.02, -66.6) * mm});
            skArc(sketch, "E11.30.0", {"start": v(-39.81, -67.93) * mm, "mid": v(-39.43, -67.99) * mm, "end": v(-39.12, -67.75) * mm});
            skLineSegment(sketch, "E11.30.1", {"start": v(-38.1, -66) * mm, "end": v(-39.12, -67.75) * mm});
            skArc(sketch, "E11.30.2", {"start": v(-38.1, -66) * mm, "mid": v(-37.1, -65.24) * mm, "end": v(-36.06, -64.55) * mm});
            skArc(sketch, "E11.30.3", {"start": v(-35.54, -64.55) * mm, "mid": v(-35.8, -64.48) * mm, "end": v(-36.06, -64.55) * mm});
            skLineSegment(sketch, "E11.30.4", {"start": v(-35.54, -64.55) * mm, "end": v(-35.35, -64.66) * mm});
            skLineSegment(sketch, "E11.30.5", {"start": v(-35.16, -64.78) * mm, "end": v(-35.35, -64.66) * mm});
            skArc(sketch, "E11.30.6", {"start": v(-34.92, -65.24) * mm, "mid": v(-34.98, -64.98) * mm, "end": v(-35.16, -64.78) * mm});
            skArc(sketch, "E11.30.7", {"start": v(-35.26, -67.72) * mm, "mid": v(-35.05, -66.48) * mm, "end": v(-34.92, -65.24) * mm});
            skLineSegment(sketch, "E11.30.8", {"start": v(-35.26, -67.72) * mm, "end": v(-36.25, -69.28) * mm});
            skArc(sketch, "E11.30.9", {"start": v(-36.25, -69.28) * mm, "mid": v(-36.31, -69.68) * mm, "end": v(-36.06, -70) * mm});
            skArc(sketch, "E11.31.0", {"start": v(-33.74, -71.15) * mm, "mid": v(-33.35, -71.16) * mm, "end": v(-33.06, -70.9) * mm});
            skLineSegment(sketch, "E11.31.1", {"start": v(-32.2, -69.06) * mm, "end": v(-33.06, -70.9) * mm});
            skArc(sketch, "E11.31.2", {"start": v(-32.2, -69.06) * mm, "mid": v(-31.28, -68.22) * mm, "end": v(-30.3, -67.45) * mm});
            skArc(sketch, "E11.31.3", {"start": v(-29.78, -67.4) * mm, "mid": v(-30.05, -67.35) * mm, "end": v(-30.3, -67.45) * mm});
            skLineSegment(sketch, "E11.31.4", {"start": v(-29.78, -67.4) * mm, "end": v(-29.58, -67.5) * mm});
            skLineSegment(sketch, "E11.31.5", {"start": v(-29.38, -67.6) * mm, "end": v(-29.58, -67.5) * mm});
            skArc(sketch, "E11.31.6", {"start": v(-29.1, -68.04) * mm, "mid": v(-29.18, -67.78) * mm, "end": v(-29.38, -67.6) * mm});
            skArc(sketch, "E11.31.7", {"start": v(-29.22, -70.53) * mm, "mid": v(-29.12, -69.29) * mm, "end": v(-29.1, -68.04) * mm});
            skLineSegment(sketch, "E11.31.8", {"start": v(-29.22, -70.53) * mm, "end": v(-30.08, -72.17) * mm});
            skArc(sketch, "E11.31.9", {"start": v(-30.08, -72.17) * mm, "mid": v(-30.1, -72.58) * mm, "end": v(-29.82, -72.88) * mm});
            skArc(sketch, "E11.32.0", {"start": v(-27.41, -73.81) * mm, "mid": v(-27.02, -73.8) * mm, "end": v(-26.76, -73.51) * mm});
            skLineSegment(sketch, "E11.32.1", {"start": v(-26.06, -71.6) * mm, "end": v(-26.76, -73.51) * mm});
            skArc(sketch, "E11.32.2", {"start": v(-26.06, -71.6) * mm, "mid": v(-25.21, -70.7) * mm, "end": v(-24.3, -69.83) * mm});
            skArc(sketch, "E11.32.3", {"start": v(-23.8, -69.74) * mm, "mid": v(-24.06, -69.72) * mm, "end": v(-24.3, -69.83) * mm});
            skLineSegment(sketch, "E11.32.4", {"start": v(-23.8, -69.74) * mm, "end": v(-23.58, -69.81) * mm});
            skLineSegment(sketch, "E11.32.5", {"start": v(-23.37, -69.9) * mm, "end": v(-23.58, -69.81) * mm});
            skArc(sketch, "E11.32.6", {"start": v(-23.06, -70.32) * mm, "mid": v(-23.16, -70.07) * mm, "end": v(-23.37, -69.9) * mm});
            skArc(sketch, "E11.32.7", {"start": v(-22.96, -72.8) * mm, "mid": v(-22.97, -71.56) * mm, "end": v(-23.06, -70.32) * mm});
            skLineSegment(sketch, "E11.32.8", {"start": v(-22.96, -72.8) * mm, "end": v(-23.67, -74.52) * mm});
            skArc(sketch, "E11.32.9", {"start": v(-23.67, -74.52) * mm, "mid": v(-23.66, -74.93) * mm, "end": v(-23.35, -75.2) * mm});
            skArc(sketch, "E11.33.0", {"start": v(-20.87, -75.92) * mm, "mid": v(-20.49, -75.87) * mm, "end": v(-20.25, -75.56) * mm});
            skLineSegment(sketch, "E11.33.1", {"start": v(-19.72, -73.6) * mm, "end": v(-20.25, -75.56) * mm});
            skArc(sketch, "E11.33.2", {"start": v(-19.72, -73.6) * mm, "mid": v(-18.95, -72.62) * mm, "end": v(-18.12, -71.69) * mm});
            skArc(sketch, "E11.33.3", {"start": v(-17.63, -71.55) * mm, "mid": v(-17.9, -71.55) * mm, "end": v(-18.12, -71.69) * mm});
            skLineSegment(sketch, "E11.33.4", {"start": v(-17.63, -71.55) * mm, "end": v(-17.4, -71.6) * mm});
            skLineSegment(sketch, "E11.33.5", {"start": v(-17.2, -71.67) * mm, "end": v(-17.4, -71.6) * mm});
            skArc(sketch, "E11.33.6", {"start": v(-16.85, -72.06) * mm, "mid": v(-16.97, -71.82) * mm, "end": v(-17.2, -71.67) * mm});
            skArc(sketch, "E11.33.7", {"start": v(-16.53, -74.53) * mm, "mid": v(-16.65, -73.3) * mm, "end": v(-16.85, -72.06) * mm});
            skLineSegment(sketch, "E11.33.8", {"start": v(-16.53, -74.53) * mm, "end": v(-17.09, -76.3) * mm});
            skArc(sketch, "E11.33.9", {"start": v(-17.09, -76.3) * mm, "mid": v(-17.04, -76.7) * mm, "end": v(-16.7, -76.95) * mm});
            skArc(sketch, "E11.34.0", {"start": v(-14.18, -77.45) * mm, "mid": v(-13.8, -77.37) * mm, "end": v(-13.58, -77.04) * mm});
            skLineSegment(sketch, "E11.34.1", {"start": v(-13.23, -75.04) * mm, "end": v(-13.58, -77.04) * mm});
            skArc(sketch, "E11.34.2", {"start": v(-13.23, -75.04) * mm, "mid": v(-12.55, -74) * mm, "end": v(-11.8, -73) * mm});
            skArc(sketch, "E11.34.3", {"start": v(-11.32, -72.8) * mm, "mid": v(-11.6, -72.83) * mm, "end": v(-11.8, -73) * mm});
            skLineSegment(sketch, "E11.34.4", {"start": v(-11.32, -72.8) * mm, "end": v(-11.1, -72.85) * mm});
            skLineSegment(sketch, "E11.34.5", {"start": v(-10.88, -72.9) * mm, "end": v(-11.1, -72.85) * mm});
            skArc(sketch, "E11.34.6", {"start": v(-10.5, -73.25) * mm, "mid": v(-10.64, -73.02) * mm, "end": v(-10.88, -72.9) * mm});
            skArc(sketch, "E11.34.7", {"start": v(-9.97, -75.7) * mm, "mid": v(-10.2, -74.46) * mm, "end": v(-10.5, -73.25) * mm});
            skLineSegment(sketch, "E11.34.8", {"start": v(-9.97, -75.7) * mm, "end": v(-10.37, -77.5) * mm});
            skArc(sketch, "E11.34.9", {"start": v(-10.37, -77.5) * mm, "mid": v(-10.3, -77.9) * mm, "end": v(-9.94, -78.11) * mm});
            skArc(sketch, "E11.35.0", {"start": v(-7.37, -78.4) * mm, "mid": v(-7, -78.28) * mm, "end": v(-6.82, -77.93) * mm});
            skLineSegment(sketch, "E11.35.1", {"start": v(-6.64, -75.91) * mm, "end": v(-6.82, -77.93) * mm});
            skArc(sketch, "E11.35.2", {"start": v(-6.64, -75.91) * mm, "mid": v(-6.06, -74.8) * mm, "end": v(-5.4, -73.74) * mm});
            skArc(sketch, "E11.35.3", {"start": v(-4.93, -73.52) * mm, "mid": v(-5.2, -73.57) * mm, "end": v(-5.4, -73.74) * mm});
            skLineSegment(sketch, "E11.35.4", {"start": v(-4.93, -73.52) * mm, "end": v(-4.7, -73.54) * mm});
            skLineSegment(sketch, "E11.35.5", {"start": v(-4.49, -73.57) * mm, "end": v(-4.7, -73.54) * mm});
            skArc(sketch, "E11.35.6", {"start": v(-4.08, -73.89) * mm, "mid": v(-4.24, -73.67) * mm, "end": v(-4.49, -73.57) * mm});
            skArc(sketch, "E11.35.7", {"start": v(-3.34, -76.27) * mm, "mid": v(-3.67, -75.07) * mm, "end": v(-4.08, -73.89) * mm});
            skLineSegment(sketch, "E11.35.8", {"start": v(-3.34, -76.27) * mm, "end": v(-3.58, -78.1) * mm});
            skArc(sketch, "E11.35.9", {"start": v(-3.58, -78.1) * mm, "mid": v(-3.46, -78.5) * mm, "end": v(-3.1, -78.68) * mm});
            skArc(sketch, "E11.36.0", {"start": v(-0.51, -78.74) * mm, "mid": v(-0.15, -78.6) * mm, "end": v(0, -78.23) * mm});
            skLineSegment(sketch, "E11.36.1", {"start": v(0, -76.2) * mm, "end": v(0, -78.23) * mm});
            skArc(sketch, "E11.36.2", {"start": v(0, -76.2) * mm, "mid": v(0.49, -75.05) * mm, "end": v(1.05, -73.93) * mm});
            skArc(sketch, "E11.36.3", {"start": v(1.5, -73.67) * mm, "mid": v(1.23, -73.74) * mm, "end": v(1.05, -73.93) * mm});
            skLineSegment(sketch, "E11.36.4", {"start": v(1.5, -73.67) * mm, "end": v(1.72, -73.67) * mm});
            skLineSegment(sketch, "E11.36.5", {"start": v(1.94, -73.68) * mm, "end": v(1.72, -73.67) * mm});
            skArc(sketch, "E11.36.6", {"start": v(2.38, -73.96) * mm, "mid": v(2.2, -73.76) * mm, "end": v(1.94, -73.68) * mm});
            skArc(sketch, "E11.36.7", {"start": v(3.32, -76.27) * mm, "mid": v(2.89, -75.1) * mm, "end": v(2.38, -73.96) * mm});
            skLineSegment(sketch, "E11.36.8", {"start": v(3.32, -76.27) * mm, "end": v(3.24, -78.12) * mm});
            skArc(sketch, "E11.36.9", {"start": v(3.24, -78.12) * mm, "mid": v(3.4, -78.5) * mm, "end": v(3.78, -78.65) * mm});
            skArc(sketch, "E11.37.0", {"start": v(6.35, -78.48) * mm, "mid": v(6.7, -78.3) * mm, "end": v(6.82, -77.93) * mm});
            skLineSegment(sketch, "E11.37.1", {"start": v(6.64, -75.91) * mm, "end": v(6.82, -77.93) * mm});
            skArc(sketch, "E11.37.2", {"start": v(6.64, -75.91) * mm, "mid": v(7.03, -74.72) * mm, "end": v(7.49, -73.56) * mm});
            skArc(sketch, "E11.37.3", {"start": v(7.9, -73.26) * mm, "mid": v(7.66, -73.35) * mm, "end": v(7.49, -73.56) * mm});
            skLineSegment(sketch, "E11.37.4", {"start": v(7.9, -73.26) * mm, "end": v(8.13, -73.24) * mm});
            skLineSegment(sketch, "E11.37.5", {"start": v(8.36, -73.23) * mm, "end": v(8.13, -73.24) * mm});
            skArc(sketch, "E11.37.6", {"start": v(8.81, -73.47) * mm, "mid": v(8.62, -73.29) * mm, "end": v(8.36, -73.23) * mm});
            skArc(sketch, "E11.37.7", {"start": v(9.96, -75.7) * mm, "mid": v(9.42, -74.56) * mm, "end": v(8.81, -73.47) * mm});
            skLineSegment(sketch, "E11.37.8", {"start": v(9.96, -75.7) * mm, "end": v(10.04, -77.54) * mm});
            skArc(sketch, "E11.37.9", {"start": v(10.04, -77.54) * mm, "mid": v(10.22, -77.9) * mm, "end": v(10.62, -78.02) * mm});
            skArc(sketch, "E11.38.0", {"start": v(13.17, -77.63) * mm, "mid": v(13.5, -77.42) * mm, "end": v(13.58, -77.04) * mm});
            skLineSegment(sketch, "E11.38.1", {"start": v(13.23, -75.04) * mm, "end": v(13.58, -77.04) * mm});
            skArc(sketch, "E11.38.2", {"start": v(13.23, -75.04) * mm, "mid": v(13.51, -73.83) * mm, "end": v(13.87, -72.63) * mm});
            skArc(sketch, "E11.38.3", {"start": v(14.26, -72.3) * mm, "mid": v(14.02, -72.4) * mm, "end": v(13.87, -72.63) * mm});
            skLineSegment(sketch, "E11.38.4", {"start": v(14.26, -72.3) * mm, "end": v(14.48, -72.25) * mm});
            skLineSegment(sketch, "E11.38.5", {"start": v(14.7, -72.22) * mm, "end": v(14.48, -72.25) * mm});
            skArc(sketch, "E11.38.6", {"start": v(15.18, -72.43) * mm, "mid": v(14.97, -72.26) * mm, "end": v(14.7, -72.22) * mm});
            skArc(sketch, "E11.38.7", {"start": v(16.52, -74.54) * mm, "mid": v(15.89, -73.46) * mm, "end": v(15.18, -72.43) * mm});
            skLineSegment(sketch, "E11.38.8", {"start": v(16.52, -74.54) * mm, "end": v(16.76, -76.37) * mm});
            skArc(sketch, "E11.38.9", {"start": v(16.76, -76.37) * mm, "mid": v(16.97, -76.72) * mm, "end": v(17.37, -76.8) * mm});
            skArc(sketch, "E11.39.0", {"start": v(19.89, -76.19) * mm, "mid": v(20.2, -75.95) * mm, "end": v(20.25, -75.56) * mm});
            skLineSegment(sketch, "E11.39.1", {"start": v(19.72, -73.6) * mm, "end": v(20.25, -75.56) * mm});
            skArc(sketch, "E11.39.2", {"start": v(19.72, -73.6) * mm, "mid": v(19.9, -72.37) * mm, "end": v(20.15, -71.14) * mm});
            skArc(sketch, "E11.39.3", {"start": v(20.5, -70.77) * mm, "mid": v(20.28, -70.9) * mm, "end": v(20.15, -71.14) * mm});
            skLineSegment(sketch, "E11.39.4", {"start": v(20.5, -70.77) * mm, "end": v(20.73, -70.71) * mm});
            skLineSegment(sketch, "E11.39.5", {"start": v(20.95, -70.67) * mm, "end": v(20.73, -70.71) * mm});
            skArc(sketch, "E11.39.6", {"start": v(21.44, -70.83) * mm, "mid": v(21.21, -70.68) * mm, "end": v(20.95, -70.67) * mm});
            skArc(sketch, "E11.39.7", {"start": v(22.95, -72.81) * mm, "mid": v(22.23, -71.8) * mm, "end": v(21.44, -70.83) * mm});
            skLineSegment(sketch, "E11.39.8", {"start": v(22.95, -72.81) * mm, "end": v(23.35, -74.62) * mm});
            skArc(sketch, "E11.39.9", {"start": v(23.35, -74.62) * mm, "mid": v(23.6, -74.95) * mm, "end": v(24, -75) * mm});
            skArc(sketch, "E11.40.0", {"start": v(26.45, -74.16) * mm, "mid": v(26.74, -73.9) * mm, "end": v(26.76, -73.51) * mm});
            skLineSegment(sketch, "E11.40.1", {"start": v(26.06, -71.6) * mm, "end": v(26.76, -73.51) * mm});
            skArc(sketch, "E11.40.2", {"start": v(26.06, -71.6) * mm, "mid": v(26.13, -70.36) * mm, "end": v(26.27, -69.12) * mm});
            skArc(sketch, "E11.40.3", {"start": v(26.6, -68.72) * mm, "mid": v(26.38, -68.87) * mm, "end": v(26.27, -69.12) * mm});
            skLineSegment(sketch, "E11.40.4", {"start": v(26.6, -68.72) * mm, "end": v(26.81, -68.64) * mm});
            skLineSegment(sketch, "E11.40.5", {"start": v(27.03, -68.57) * mm, "end": v(26.81, -68.64) * mm});
            skArc(sketch, "E11.40.6", {"start": v(27.53, -68.69) * mm, "mid": v(27.3, -68.56) * mm, "end": v(27.03, -68.57) * mm});
            skArc(sketch, "E11.40.7", {"start": v(29.21, -70.54) * mm, "mid": v(28.4, -69.59) * mm, "end": v(27.53, -68.69) * mm});
            skLineSegment(sketch, "E11.40.8", {"start": v(29.21, -70.54) * mm, "end": v(29.77, -72.3) * mm});
            skArc(sketch, "E11.40.9", {"start": v(29.77, -72.3) * mm, "mid": v(30.04, -72.6) * mm, "end": v(30.45, -72.62) * mm});
            skArc(sketch, "E11.41.0", {"start": v(32.81, -71.58) * mm, "mid": v(33.08, -71.3) * mm, "end": v(33.06, -70.9) * mm});
            skLineSegment(sketch, "E11.41.1", {"start": v(32.2, -69.06) * mm, "end": v(33.06, -70.9) * mm});
            skArc(sketch, "E11.41.2", {"start": v(32.2, -69.06) * mm, "mid": v(32.16, -67.81) * mm, "end": v(32.2, -66.56) * mm});
            skArc(sketch, "E11.41.3", {"start": v(32.49, -66.14) * mm, "mid": v(32.28, -66.31) * mm, "end": v(32.2, -66.56) * mm});
            skLineSegment(sketch, "E11.41.4", {"start": v(32.49, -66.14) * mm, "end": v(32.7, -66.04) * mm});
            skLineSegment(sketch, "E11.41.5", {"start": v(32.9, -65.95) * mm, "end": v(32.7, -66.04) * mm});
            skArc(sketch, "E11.41.6", {"start": v(33.41, -66.03) * mm, "mid": v(33.17, -65.92) * mm, "end": v(32.9, -65.95) * mm});
            skArc(sketch, "E11.41.7", {"start": v(35.25, -67.72) * mm, "mid": v(34.36, -66.85) * mm, "end": v(33.41, -66.03) * mm});
            skLineSegment(sketch, "E11.41.8", {"start": v(35.25, -67.72) * mm, "end": v(35.95, -69.43) * mm});
            skArc(sketch, "E11.41.9", {"start": v(35.95, -69.43) * mm, "mid": v(36.25, -69.71) * mm, "end": v(36.66, -69.69) * mm});
            skArc(sketch, "E11.42.0", {"start": v(38.93, -68.45) * mm, "mid": v(39.17, -68.14) * mm, "end": v(39.12, -67.75) * mm});
            skLineSegment(sketch, "E11.42.1", {"start": v(38.1, -66) * mm, "end": v(39.12, -67.75) * mm});
            skArc(sketch, "E11.42.2", {"start": v(38.1, -66) * mm, "mid": v(37.95, -64.75) * mm, "end": v(37.87, -63.5) * mm});
            skArc(sketch, "E11.42.3", {"start": v(38.13, -63.05) * mm, "mid": v(37.94, -63.24) * mm, "end": v(37.87, -63.5) * mm});
            skLineSegment(sketch, "E11.42.4", {"start": v(38.13, -63.05) * mm, "end": v(38.32, -62.94) * mm});
            skLineSegment(sketch, "E11.42.5", {"start": v(38.52, -62.84) * mm, "end": v(38.32, -62.94) * mm});
            skArc(sketch, "E11.42.6", {"start": v(39.04, -62.87) * mm, "mid": v(38.79, -62.78) * mm, "end": v(38.52, -62.84) * mm});
            skArc(sketch, "E11.42.7", {"start": v(41.01, -64.4) * mm, "mid": v(40.05, -63.6) * mm, "end": v(39.04, -62.87) * mm});
            skLineSegment(sketch, "E11.42.8", {"start": v(41.01, -64.4) * mm, "end": v(41.87, -66.03) * mm});
            skArc(sketch, "E11.42.9", {"start": v(41.87, -66.03) * mm, "mid": v(42.19, -66.29) * mm, "end": v(42.6, -66.22) * mm});
            skArc(sketch, "E11.43.0", {"start": v(44.74, -64.8) * mm, "mid": v(44.95, -64.46) * mm, "end": v(44.87, -64.08) * mm});
            skLineSegment(sketch, "E11.43.1", {"start": v(43.7, -62.42) * mm, "end": v(44.87, -64.08) * mm});
            skArc(sketch, "E11.43.2", {"start": v(43.7, -62.42) * mm, "mid": v(43.45, -61.2) * mm, "end": v(43.26, -59.96) * mm});
            skArc(sketch, "E11.43.3", {"start": v(43.48, -59.49) * mm, "mid": v(43.3, -59.7) * mm, "end": v(43.26, -59.96) * mm});
            skLineSegment(sketch, "E11.43.4", {"start": v(43.48, -59.49) * mm, "end": v(43.66, -59.36) * mm});
            skLineSegment(sketch, "E11.43.5", {"start": v(43.85, -59.24) * mm, "end": v(43.66, -59.36) * mm});
            skArc(sketch, "E11.43.6", {"start": v(44.37, -59.22) * mm, "mid": v(44.1, -59.16) * mm, "end": v(43.85, -59.24) * mm});
            skArc(sketch, "E11.43.7", {"start": v(46.47, -60.57) * mm, "mid": v(45.44, -59.86) * mm, "end": v(44.37, -59.22) * mm});
            skLineSegment(sketch, "E11.43.8", {"start": v(46.47, -60.57) * mm, "end": v(47.46, -62.13) * mm});
            skArc(sketch, "E11.43.9", {"start": v(47.46, -62.13) * mm, "mid": v(47.8, -62.36) * mm, "end": v(48.2, -62.26) * mm});
            skArc(sketch, "E11.44.0", {"start": v(50.22, -60.65) * mm, "mid": v(50.4, -60.3) * mm, "end": v(50.29, -59.93) * mm});
            skLineSegment(sketch, "E11.44.1", {"start": v(48.98, -58.37) * mm, "end": v(50.29, -59.93) * mm});
            skArc(sketch, "E11.44.2", {"start": v(48.98, -58.37) * mm, "mid": v(48.61, -57.18) * mm, "end": v(48.33, -55.96) * mm});
            skArc(sketch, "E11.44.3", {"start": v(48.5, -55.47) * mm, "mid": v(48.34, -55.7) * mm, "end": v(48.33, -55.96) * mm});
            skLineSegment(sketch, "E11.44.4", {"start": v(48.5, -55.47) * mm, "end": v(48.67, -55.33) * mm});
            skLineSegment(sketch, "E11.44.5", {"start": v(48.85, -55.2) * mm, "end": v(48.67, -55.33) * mm});
            skArc(sketch, "E11.44.6", {"start": v(49.36, -55.13) * mm, "mid": v(49.1, -55.1) * mm, "end": v(48.85, -55.2) * mm});
            skArc(sketch, "E11.44.7", {"start": v(51.57, -56.3) * mm, "mid": v(50.49, -55.68) * mm, "end": v(49.36, -55.13) * mm});
            skLineSegment(sketch, "E11.44.8", {"start": v(51.57, -56.3) * mm, "end": v(52.7, -57.76) * mm});
            skArc(sketch, "E11.44.9", {"start": v(52.7, -57.76) * mm, "mid": v(53.06, -57.96) * mm, "end": v(53.45, -57.82) * mm});
            skArc(sketch, "E11.45.0", {"start": v(55.31, -56.04) * mm, "mid": v(55.47, -55.68) * mm, "end": v(55.32, -55.32) * mm});
            skLineSegment(sketch, "E11.45.1", {"start": v(53.88, -53.88) * mm, "end": v(55.32, -55.32) * mm});
            skArc(sketch, "E11.45.2", {"start": v(53.88, -53.88) * mm, "mid": v(53.41, -52.72) * mm, "end": v(53.02, -51.54) * mm});
            skArc(sketch, "E11.45.3", {"start": v(53.15, -51.04) * mm, "mid": v(53.01, -51.27) * mm, "end": v(53.02, -51.54) * mm});
            skLineSegment(sketch, "E11.45.4", {"start": v(53.15, -51.04) * mm, "end": v(53.3, -50.88) * mm});
            skLineSegment(sketch, "E11.45.5", {"start": v(53.47, -50.73) * mm, "end": v(53.3, -50.88) * mm});
            skArc(sketch, "E11.45.6", {"start": v(53.98, -50.62) * mm, "mid": v(53.71, -50.6) * mm, "end": v(53.47, -50.73) * mm});
            skArc(sketch, "E11.45.7", {"start": v(56.28, -51.58) * mm, "mid": v(55.15, -51.06) * mm, "end": v(53.98, -50.62) * mm});
            skLineSegment(sketch, "E11.45.8", {"start": v(56.28, -51.58) * mm, "end": v(57.53, -52.95) * mm});
            skArc(sketch, "E11.45.9", {"start": v(57.53, -52.95) * mm, "mid": v(57.9, -53.11) * mm, "end": v(58.28, -52.94) * mm});
            skArc(sketch, "E11.46.0", {"start": v(59.99, -51) * mm, "mid": v(60.1, -50.63) * mm, "end": v(59.93, -50.29) * mm});
            skLineSegment(sketch, "E11.46.1", {"start": v(58.37, -48.98) * mm, "end": v(59.93, -50.29) * mm});
            skArc(sketch, "E11.46.2", {"start": v(58.37, -48.98) * mm, "mid": v(57.8, -47.87) * mm, "end": v(57.3, -46.72) * mm});
            skArc(sketch, "E11.46.3", {"start": v(57.4, -46.21) * mm, "mid": v(57.28, -46.45) * mm, "end": v(57.3, -46.72) * mm});
            skLineSegment(sketch, "E11.46.4", {"start": v(57.4, -46.21) * mm, "end": v(57.54, -46.04) * mm});
            skLineSegment(sketch, "E11.46.5", {"start": v(57.7, -45.87) * mm, "end": v(57.54, -46.04) * mm});
            skArc(sketch, "E11.46.6", {"start": v(58.19, -45.72) * mm, "mid": v(57.92, -45.73) * mm, "end": v(57.7, -45.87) * mm});
            skArc(sketch, "E11.46.7", {"start": v(60.56, -46.48) * mm, "mid": v(59.39, -46.06) * mm, "end": v(58.19, -45.72) * mm});
            skLineSegment(sketch, "E11.46.8", {"start": v(60.56, -46.48) * mm, "end": v(61.93, -47.73) * mm});
            skArc(sketch, "E11.46.9", {"start": v(61.93, -47.73) * mm, "mid": v(62.32, -47.86) * mm, "end": v(62.68, -47.66) * mm});
            skArc(sketch, "E11.47.0", {"start": v(64.2, -45.58) * mm, "mid": v(64.3, -45.2) * mm, "end": v(64.08, -44.87) * mm});
            skLineSegment(sketch, "E11.47.1", {"start": v(62.42, -43.7) * mm, "end": v(64.08, -44.87) * mm});
            skArc(sketch, "E11.47.2", {"start": v(62.42, -43.7) * mm, "mid": v(61.76, -42.65) * mm, "end": v(61.16, -41.55) * mm});
            skArc(sketch, "E11.47.3", {"start": v(61.2, -41.03) * mm, "mid": v(61.11, -41.29) * mm, "end": v(61.16, -41.55) * mm});
            skLineSegment(sketch, "E11.47.4", {"start": v(61.2, -41.03) * mm, "end": v(61.33, -40.85) * mm});
            skLineSegment(sketch, "E11.47.5", {"start": v(61.47, -40.67) * mm, "end": v(61.33, -40.85) * mm});
            skArc(sketch, "E11.47.6", {"start": v(61.95, -40.48) * mm, "mid": v(61.68, -40.5) * mm, "end": v(61.47, -40.67) * mm});
            skArc(sketch, "E11.47.7", {"start": v(64.39, -41.03) * mm, "mid": v(63.18, -40.71) * mm, "end": v(61.95, -40.48) * mm});
            skLineSegment(sketch, "E11.47.8", {"start": v(64.39, -41.03) * mm, "end": v(65.85, -42.15) * mm});
            skArc(sketch, "E11.47.9", {"start": v(65.85, -42.15) * mm, "mid": v(66.25, -42.25) * mm, "end": v(66.6, -42.02) * mm});
            skArc(sketch, "E11.48.0", {"start": v(67.93, -39.81) * mm, "mid": v(67.99, -39.43) * mm, "end": v(67.75, -39.12) * mm});
            skLineSegment(sketch, "E11.48.1", {"start": v(66, -38.1) * mm, "end": v(67.75, -39.12) * mm});
            skArc(sketch, "E11.48.2", {"start": v(66, -38.1) * mm, "mid": v(65.24, -37.1) * mm, "end": v(64.55, -36.06) * mm});
            skArc(sketch, "E11.48.3", {"start": v(64.55, -35.54) * mm, "mid": v(64.48, -35.8) * mm, "end": v(64.55, -36.06) * mm});
            skLineSegment(sketch, "E11.48.4", {"start": v(64.55, -35.54) * mm, "end": v(64.66, -35.35) * mm});
            skLineSegment(sketch, "E11.48.5", {"start": v(64.78, -35.16) * mm, "end": v(64.66, -35.35) * mm});
            skArc(sketch, "E11.48.6", {"start": v(65.24, -34.92) * mm, "mid": v(64.98, -34.98) * mm, "end": v(64.78, -35.16) * mm});
            skArc(sketch, "E11.48.7", {"start": v(67.72, -35.26) * mm, "mid": v(66.48, -35.05) * mm, "end": v(65.24, -34.92) * mm});
            skLineSegment(sketch, "E11.48.8", {"start": v(67.72, -35.26) * mm, "end": v(69.28, -36.25) * mm});
            skArc(sketch, "E11.48.9", {"start": v(69.28, -36.25) * mm, "mid": v(69.68, -36.31) * mm, "end": v(70, -36.06) * mm});
            skArc(sketch, "E11.49.0", {"start": v(71.15, -33.74) * mm, "mid": v(71.16, -33.35) * mm, "end": v(70.9, -33.06) * mm});
            skLineSegment(sketch, "E11.49.1", {"start": v(69.06, -32.2) * mm, "end": v(70.9, -33.06) * mm});
            skArc(sketch, "E11.49.2", {"start": v(69.06, -32.2) * mm, "mid": v(68.22, -31.28) * mm, "end": v(67.45, -30.3) * mm});
            skArc(sketch, "E11.49.3", {"start": v(67.4, -29.78) * mm, "mid": v(67.35, -30.05) * mm, "end": v(67.45, -30.3) * mm});
            skLineSegment(sketch, "E11.49.4", {"start": v(67.4, -29.78) * mm, "end": v(67.5, -29.58) * mm});
            skLineSegment(sketch, "E11.49.5", {"start": v(67.6, -29.38) * mm, "end": v(67.5, -29.58) * mm});
            skArc(sketch, "E11.49.6", {"start": v(68.04, -29.1) * mm, "mid": v(67.78, -29.18) * mm, "end": v(67.6, -29.38) * mm});
            skArc(sketch, "E11.49.7", {"start": v(70.53, -29.22) * mm, "mid": v(69.29, -29.12) * mm, "end": v(68.04, -29.1) * mm});
            skLineSegment(sketch, "E11.49.8", {"start": v(70.53, -29.22) * mm, "end": v(72.17, -30.08) * mm});
            skArc(sketch, "E11.49.9", {"start": v(72.17, -30.08) * mm, "mid": v(72.58, -30.1) * mm, "end": v(72.88, -29.82) * mm});
            skArc(sketch, "E11.50.0", {"start": v(73.81, -27.41) * mm, "mid": v(73.8, -27.02) * mm, "end": v(73.51, -26.76) * mm});
            skLineSegment(sketch, "E11.50.1", {"start": v(71.6, -26.06) * mm, "end": v(73.51, -26.76) * mm});
            skArc(sketch, "E11.50.2", {"start": v(71.6, -26.06) * mm, "mid": v(70.7, -25.21) * mm, "end": v(69.83, -24.3) * mm});
            skArc(sketch, "E11.50.3", {"start": v(69.74, -23.8) * mm, "mid": v(69.72, -24.06) * mm, "end": v(69.83, -24.3) * mm});
            skLineSegment(sketch, "E11.50.4", {"start": v(69.74, -23.8) * mm, "end": v(69.81, -23.58) * mm});
            skLineSegment(sketch, "E11.50.5", {"start": v(69.9, -23.37) * mm, "end": v(69.81, -23.58) * mm});
            skArc(sketch, "E11.50.6", {"start": v(70.32, -23.06) * mm, "mid": v(70.07, -23.16) * mm, "end": v(69.9, -23.37) * mm});
            skArc(sketch, "E11.50.7", {"start": v(72.8, -22.96) * mm, "mid": v(71.56, -22.97) * mm, "end": v(70.32, -23.06) * mm});
            skLineSegment(sketch, "E11.50.8", {"start": v(72.8, -22.96) * mm, "end": v(74.52, -23.67) * mm});
            skArc(sketch, "E11.50.9", {"start": v(74.52, -23.67) * mm, "mid": v(74.93, -23.66) * mm, "end": v(75.2, -23.35) * mm});
            skArc(sketch, "E11.51.0", {"start": v(75.92, -20.87) * mm, "mid": v(75.87, -20.49) * mm, "end": v(75.56, -20.25) * mm});
            skLineSegment(sketch, "E11.51.1", {"start": v(73.6, -19.72) * mm, "end": v(75.56, -20.25) * mm});
            skArc(sketch, "E11.51.2", {"start": v(73.6, -19.72) * mm, "mid": v(72.62, -18.95) * mm, "end": v(71.69, -18.12) * mm});
            skArc(sketch, "E11.51.3", {"start": v(71.55, -17.63) * mm, "mid": v(71.55, -17.9) * mm, "end": v(71.69, -18.12) * mm});
            skLineSegment(sketch, "E11.51.4", {"start": v(71.55, -17.63) * mm, "end": v(71.6, -17.4) * mm});
            skLineSegment(sketch, "E11.51.5", {"start": v(71.67, -17.2) * mm, "end": v(71.6, -17.4) * mm});
            skArc(sketch, "E11.51.6", {"start": v(72.06, -16.85) * mm, "mid": v(71.82, -16.97) * mm, "end": v(71.67, -17.2) * mm});
            skArc(sketch, "E11.51.7", {"start": v(74.53, -16.53) * mm, "mid": v(73.3, -16.65) * mm, "end": v(72.06, -16.85) * mm});
            skLineSegment(sketch, "E11.51.8", {"start": v(74.53, -16.53) * mm, "end": v(76.3, -17.09) * mm});
            skArc(sketch, "E11.51.9", {"start": v(76.3, -17.09) * mm, "mid": v(76.7, -17.04) * mm, "end": v(76.95, -16.7) * mm});
            skArc(sketch, "E11.52.0", {"start": v(77.45, -14.18) * mm, "mid": v(77.37, -13.8) * mm, "end": v(77.04, -13.58) * mm});
            skLineSegment(sketch, "E11.52.1", {"start": v(75.04, -13.23) * mm, "end": v(77.04, -13.58) * mm});
            skArc(sketch, "E11.52.2", {"start": v(75.04, -13.23) * mm, "mid": v(74, -12.55) * mm, "end": v(73, -11.8) * mm});
            skArc(sketch, "E11.52.3", {"start": v(72.8, -11.32) * mm, "mid": v(72.83, -11.6) * mm, "end": v(73, -11.8) * mm});
            skLineSegment(sketch, "E11.52.4", {"start": v(72.8, -11.32) * mm, "end": v(72.85, -11.1) * mm});
            skLineSegment(sketch, "E11.52.5", {"start": v(72.9, -10.88) * mm, "end": v(72.85, -11.1) * mm});
            skArc(sketch, "E11.52.6", {"start": v(73.25, -10.5) * mm, "mid": v(73.02, -10.64) * mm, "end": v(72.9, -10.88) * mm});
            skArc(sketch, "E11.52.7", {"start": v(75.7, -9.97) * mm, "mid": v(74.46, -10.2) * mm, "end": v(73.25, -10.5) * mm});
            skLineSegment(sketch, "E11.52.8", {"start": v(75.7, -9.97) * mm, "end": v(77.5, -10.37) * mm});
            skArc(sketch, "E11.52.9", {"start": v(77.5, -10.37) * mm, "mid": v(77.9, -10.3) * mm, "end": v(78.11, -9.94) * mm});
            skArc(sketch, "E11.53.0", {"start": v(78.4, -7.37) * mm, "mid": v(78.28, -7) * mm, "end": v(77.93, -6.82) * mm});
            skLineSegment(sketch, "E11.53.1", {"start": v(75.91, -6.64) * mm, "end": v(77.93, -6.82) * mm});
            skArc(sketch, "E11.53.2", {"start": v(75.91, -6.64) * mm, "mid": v(74.8, -6.06) * mm, "end": v(73.74, -5.4) * mm});
            skArc(sketch, "E11.53.3", {"start": v(73.52, -4.93) * mm, "mid": v(73.57, -5.2) * mm, "end": v(73.74, -5.4) * mm});
            skLineSegment(sketch, "E11.53.4", {"start": v(73.52, -4.93) * mm, "end": v(73.54, -4.7) * mm});
            skLineSegment(sketch, "E11.53.5", {"start": v(73.57, -4.49) * mm, "end": v(73.54, -4.7) * mm});
            skArc(sketch, "E11.53.6", {"start": v(73.89, -4.08) * mm, "mid": v(73.67, -4.24) * mm, "end": v(73.57, -4.49) * mm});
            skArc(sketch, "E11.53.7", {"start": v(76.27, -3.34) * mm, "mid": v(75.07, -3.67) * mm, "end": v(73.89, -4.08) * mm});
            skLineSegment(sketch, "E11.53.8", {"start": v(76.27, -3.34) * mm, "end": v(78.1, -3.58) * mm});
            skArc(sketch, "E11.53.9", {"start": v(78.1, -3.58) * mm, "mid": v(78.5, -3.46) * mm, "end": v(78.68, -3.1) * mm});
            skArc(sketch, "E11.54.0", {"start": v(78.74, -0.51) * mm, "mid": v(78.6, -0.15) * mm, "end": v(78.23, 0) * mm});
            skLineSegment(sketch, "E11.54.1", {"start": v(76.2, 0) * mm, "end": v(78.23, 0) * mm});
            skArc(sketch, "E11.54.2", {"start": v(76.2, 0) * mm, "mid": v(75.05, 0.49) * mm, "end": v(73.93, 1.05) * mm});
            skArc(sketch, "E11.54.3", {"start": v(73.67, 1.5) * mm, "mid": v(73.74, 1.23) * mm, "end": v(73.93, 1.05) * mm});
            skLineSegment(sketch, "E11.54.4", {"start": v(73.67, 1.5) * mm, "end": v(73.67, 1.72) * mm});
            skLineSegment(sketch, "E11.54.5", {"start": v(73.68, 1.94) * mm, "end": v(73.67, 1.72) * mm});
            skArc(sketch, "E11.54.6", {"start": v(73.96, 2.38) * mm, "mid": v(73.76, 2.2) * mm, "end": v(73.68, 1.94) * mm});
            skArc(sketch, "E11.54.7", {"start": v(76.27, 3.32) * mm, "mid": v(75.1, 2.89) * mm, "end": v(73.96, 2.38) * mm});
            skLineSegment(sketch, "E11.54.8", {"start": v(76.27, 3.32) * mm, "end": v(78.12, 3.24) * mm});
            skArc(sketch, "E11.54.9", {"start": v(78.12, 3.24) * mm, "mid": v(78.5, 3.4) * mm, "end": v(78.65, 3.78) * mm});
            skArc(sketch, "E11.55.0", {"start": v(78.48, 6.35) * mm, "mid": v(78.3, 6.7) * mm, "end": v(77.93, 6.82) * mm});
            skLineSegment(sketch, "E11.55.1", {"start": v(75.91, 6.64) * mm, "end": v(77.93, 6.82) * mm});
            skArc(sketch, "E11.55.2", {"start": v(75.91, 6.64) * mm, "mid": v(74.72, 7.03) * mm, "end": v(73.56, 7.49) * mm});
            skArc(sketch, "E11.55.3", {"start": v(73.26, 7.9) * mm, "mid": v(73.35, 7.66) * mm, "end": v(73.56, 7.49) * mm});
            skLineSegment(sketch, "E11.55.4", {"start": v(73.26, 7.9) * mm, "end": v(73.24, 8.13) * mm});
            skLineSegment(sketch, "E11.55.5", {"start": v(73.23, 8.36) * mm, "end": v(73.24, 8.13) * mm});
            skArc(sketch, "E11.55.6", {"start": v(73.47, 8.81) * mm, "mid": v(73.29, 8.62) * mm, "end": v(73.23, 8.36) * mm});
            skArc(sketch, "E11.55.7", {"start": v(75.7, 9.96) * mm, "mid": v(74.56, 9.42) * mm, "end": v(73.47, 8.81) * mm});
            skLineSegment(sketch, "E11.55.8", {"start": v(75.7, 9.96) * mm, "end": v(77.54, 10.04) * mm});
            skArc(sketch, "E11.55.9", {"start": v(77.54, 10.04) * mm, "mid": v(77.9, 10.22) * mm, "end": v(78.02, 10.62) * mm});
            skArc(sketch, "E11.56.0", {"start": v(77.63, 13.17) * mm, "mid": v(77.42, 13.5) * mm, "end": v(77.04, 13.58) * mm});
            skLineSegment(sketch, "E11.56.1", {"start": v(75.04, 13.23) * mm, "end": v(77.04, 13.58) * mm});
            skArc(sketch, "E11.56.2", {"start": v(75.04, 13.23) * mm, "mid": v(73.83, 13.51) * mm, "end": v(72.63, 13.87) * mm});
            skArc(sketch, "E11.56.3", {"start": v(72.3, 14.26) * mm, "mid": v(72.4, 14.02) * mm, "end": v(72.63, 13.87) * mm});
            skLineSegment(sketch, "E11.56.4", {"start": v(72.3, 14.26) * mm, "end": v(72.25, 14.48) * mm});
            skLineSegment(sketch, "E11.56.5", {"start": v(72.22, 14.7) * mm, "end": v(72.25, 14.48) * mm});
            skArc(sketch, "E11.56.6", {"start": v(72.43, 15.18) * mm, "mid": v(72.26, 14.97) * mm, "end": v(72.22, 14.7) * mm});
            skArc(sketch, "E11.56.7", {"start": v(74.54, 16.52) * mm, "mid": v(73.46, 15.89) * mm, "end": v(72.43, 15.18) * mm});
            skLineSegment(sketch, "E11.56.8", {"start": v(74.54, 16.52) * mm, "end": v(76.37, 16.76) * mm});
            skArc(sketch, "E11.56.9", {"start": v(76.37, 16.76) * mm, "mid": v(76.72, 16.97) * mm, "end": v(76.8, 17.37) * mm});
            skArc(sketch, "E11.57.0", {"start": v(76.19, 19.89) * mm, "mid": v(75.95, 20.2) * mm, "end": v(75.56, 20.25) * mm});
            skLineSegment(sketch, "E11.57.1", {"start": v(73.6, 19.72) * mm, "end": v(75.56, 20.25) * mm});
            skArc(sketch, "E11.57.2", {"start": v(73.6, 19.72) * mm, "mid": v(72.37, 19.9) * mm, "end": v(71.14, 20.15) * mm});
            skArc(sketch, "E11.57.3", {"start": v(70.77, 20.5) * mm, "mid": v(70.9, 20.28) * mm, "end": v(71.14, 20.15) * mm});
            skLineSegment(sketch, "E11.57.4", {"start": v(70.77, 20.5) * mm, "end": v(70.71, 20.73) * mm});
            skLineSegment(sketch, "E11.57.5", {"start": v(70.67, 20.95) * mm, "end": v(70.71, 20.73) * mm});
            skArc(sketch, "E11.57.6", {"start": v(70.83, 21.44) * mm, "mid": v(70.68, 21.21) * mm, "end": v(70.67, 20.95) * mm});
            skArc(sketch, "E11.57.7", {"start": v(72.81, 22.95) * mm, "mid": v(71.8, 22.23) * mm, "end": v(70.83, 21.44) * mm});
            skLineSegment(sketch, "E11.57.8", {"start": v(72.81, 22.95) * mm, "end": v(74.62, 23.35) * mm});
            skArc(sketch, "E11.57.9", {"start": v(74.62, 23.35) * mm, "mid": v(74.95, 23.6) * mm, "end": v(75, 24) * mm});
            skArc(sketch, "E11.58.0", {"start": v(74.16, 26.45) * mm, "mid": v(73.9, 26.74) * mm, "end": v(73.51, 26.76) * mm});
            skLineSegment(sketch, "E11.58.1", {"start": v(71.6, 26.06) * mm, "end": v(73.51, 26.76) * mm});
            skArc(sketch, "E11.58.2", {"start": v(71.6, 26.06) * mm, "mid": v(70.36, 26.13) * mm, "end": v(69.12, 26.27) * mm});
            skArc(sketch, "E11.58.3", {"start": v(68.72, 26.6) * mm, "mid": v(68.87, 26.38) * mm, "end": v(69.12, 26.27) * mm});
            skLineSegment(sketch, "E11.58.4", {"start": v(68.72, 26.6) * mm, "end": v(68.64, 26.81) * mm});
            skLineSegment(sketch, "E11.58.5", {"start": v(68.57, 27.03) * mm, "end": v(68.64, 26.81) * mm});
            skArc(sketch, "E11.58.6", {"start": v(68.69, 27.53) * mm, "mid": v(68.56, 27.3) * mm, "end": v(68.57, 27.03) * mm});
            skArc(sketch, "E11.58.7", {"start": v(70.54, 29.21) * mm, "mid": v(69.59, 28.4) * mm, "end": v(68.69, 27.53) * mm});
            skLineSegment(sketch, "E11.58.8", {"start": v(70.54, 29.21) * mm, "end": v(72.3, 29.77) * mm});
            skArc(sketch, "E11.58.9", {"start": v(72.3, 29.77) * mm, "mid": v(72.6, 30.04) * mm, "end": v(72.62, 30.45) * mm});
            skArc(sketch, "E11.59.0", {"start": v(71.58, 32.81) * mm, "mid": v(71.3, 33.08) * mm, "end": v(70.9, 33.06) * mm});
            skLineSegment(sketch, "E11.59.1", {"start": v(69.06, 32.2) * mm, "end": v(70.9, 33.06) * mm});
            skArc(sketch, "E11.59.2", {"start": v(69.06, 32.2) * mm, "mid": v(67.81, 32.16) * mm, "end": v(66.56, 32.2) * mm});
            skArc(sketch, "E11.59.3", {"start": v(66.14, 32.49) * mm, "mid": v(66.31, 32.28) * mm, "end": v(66.56, 32.2) * mm});
            skLineSegment(sketch, "E11.59.4", {"start": v(66.14, 32.49) * mm, "end": v(66.04, 32.7) * mm});
            skLineSegment(sketch, "E11.59.5", {"start": v(65.95, 32.9) * mm, "end": v(66.04, 32.7) * mm});
            skArc(sketch, "E11.59.6", {"start": v(66.03, 33.41) * mm, "mid": v(65.92, 33.17) * mm, "end": v(65.95, 32.9) * mm});
            skArc(sketch, "E11.59.7", {"start": v(67.72, 35.25) * mm, "mid": v(66.85, 34.36) * mm, "end": v(66.03, 33.41) * mm});
            skLineSegment(sketch, "E11.59.8", {"start": v(67.72, 35.25) * mm, "end": v(69.43, 35.95) * mm});
            skArc(sketch, "E11.59.9", {"start": v(69.43, 35.95) * mm, "mid": v(69.71, 36.25) * mm, "end": v(69.69, 36.66) * mm});
            skArc(sketch, "E11.60.0", {"start": v(68.45, 38.93) * mm, "mid": v(68.14, 39.17) * mm, "end": v(67.75, 39.12) * mm});
            skLineSegment(sketch, "E11.60.1", {"start": v(66, 38.1) * mm, "end": v(67.75, 39.12) * mm});
            skArc(sketch, "E11.60.2", {"start": v(66, 38.1) * mm, "mid": v(64.75, 37.95) * mm, "end": v(63.5, 37.87) * mm});
            skArc(sketch, "E11.60.3", {"start": v(63.05, 38.13) * mm, "mid": v(63.24, 37.94) * mm, "end": v(63.5, 37.87) * mm});
            skLineSegment(sketch, "E11.60.4", {"start": v(63.05, 38.13) * mm, "end": v(62.94, 38.32) * mm});
            skLineSegment(sketch, "E11.60.5", {"start": v(62.84, 38.52) * mm, "end": v(62.94, 38.32) * mm});
            skArc(sketch, "E11.60.6", {"start": v(62.87, 39.04) * mm, "mid": v(62.78, 38.79) * mm, "end": v(62.84, 38.52) * mm});
            skArc(sketch, "E11.60.7", {"start": v(64.4, 41.01) * mm, "mid": v(63.6, 40.05) * mm, "end": v(62.87, 39.04) * mm});
            skLineSegment(sketch, "E11.60.8", {"start": v(64.4, 41.01) * mm, "end": v(66.03, 41.87) * mm});
            skArc(sketch, "E11.60.9", {"start": v(66.03, 41.87) * mm, "mid": v(66.29, 42.19) * mm, "end": v(66.22, 42.6) * mm});
            skArc(sketch, "E11.61.0", {"start": v(64.8, 44.74) * mm, "mid": v(64.46, 44.95) * mm, "end": v(64.08, 44.87) * mm});
            skLineSegment(sketch, "E11.61.1", {"start": v(62.42, 43.7) * mm, "end": v(64.08, 44.87) * mm});
            skArc(sketch, "E11.61.2", {"start": v(62.42, 43.7) * mm, "mid": v(61.2, 43.45) * mm, "end": v(59.96, 43.26) * mm});
            skArc(sketch, "E11.61.3", {"start": v(59.49, 43.48) * mm, "mid": v(59.7, 43.3) * mm, "end": v(59.96, 43.26) * mm});
            skLineSegment(sketch, "E11.61.4", {"start": v(59.49, 43.48) * mm, "end": v(59.36, 43.66) * mm});
            skLineSegment(sketch, "E11.61.5", {"start": v(59.24, 43.85) * mm, "end": v(59.36, 43.66) * mm});
            skArc(sketch, "E11.61.6", {"start": v(59.22, 44.37) * mm, "mid": v(59.16, 44.1) * mm, "end": v(59.24, 43.85) * mm});
            skArc(sketch, "E11.61.7", {"start": v(60.57, 46.47) * mm, "mid": v(59.86, 45.44) * mm, "end": v(59.22, 44.37) * mm});
            skLineSegment(sketch, "E11.61.8", {"start": v(60.57, 46.47) * mm, "end": v(62.13, 47.46) * mm});
            skArc(sketch, "E11.61.9", {"start": v(62.13, 47.46) * mm, "mid": v(62.36, 47.8) * mm, "end": v(62.26, 48.2) * mm});
            skArc(sketch, "E11.62.0", {"start": v(60.65, 50.22) * mm, "mid": v(60.3, 50.4) * mm, "end": v(59.93, 50.29) * mm});
            skLineSegment(sketch, "E11.62.1", {"start": v(58.37, 48.98) * mm, "end": v(59.93, 50.29) * mm});
            skArc(sketch, "E11.62.2", {"start": v(58.37, 48.98) * mm, "mid": v(57.18, 48.61) * mm, "end": v(55.96, 48.33) * mm});
            skArc(sketch, "E11.62.3", {"start": v(55.47, 48.5) * mm, "mid": v(55.7, 48.34) * mm, "end": v(55.96, 48.33) * mm});
            skLineSegment(sketch, "E11.62.4", {"start": v(55.47, 48.5) * mm, "end": v(55.33, 48.67) * mm});
            skLineSegment(sketch, "E11.62.5", {"start": v(55.2, 48.85) * mm, "end": v(55.33, 48.67) * mm});
            skArc(sketch, "E11.62.6", {"start": v(55.13, 49.36) * mm, "mid": v(55.1, 49.1) * mm, "end": v(55.2, 48.85) * mm});
            skArc(sketch, "E11.62.7", {"start": v(56.3, 51.57) * mm, "mid": v(55.68, 50.49) * mm, "end": v(55.13, 49.36) * mm});
            skLineSegment(sketch, "E11.62.8", {"start": v(56.3, 51.57) * mm, "end": v(57.76, 52.7) * mm});
            skArc(sketch, "E11.62.9", {"start": v(57.76, 52.7) * mm, "mid": v(57.96, 53.06) * mm, "end": v(57.82, 53.45) * mm});
            skArc(sketch, "E11.63.0", {"start": v(56.04, 55.31) * mm, "mid": v(55.68, 55.47) * mm, "end": v(55.32, 55.32) * mm});
            skLineSegment(sketch, "E11.63.1", {"start": v(53.88, 53.88) * mm, "end": v(55.32, 55.32) * mm});
            skArc(sketch, "E11.63.2", {"start": v(53.88, 53.88) * mm, "mid": v(52.72, 53.41) * mm, "end": v(51.54, 53.02) * mm});
            skArc(sketch, "E11.63.3", {"start": v(51.04, 53.15) * mm, "mid": v(51.27, 53.01) * mm, "end": v(51.54, 53.02) * mm});
            skLineSegment(sketch, "E11.63.4", {"start": v(51.04, 53.15) * mm, "end": v(50.88, 53.3) * mm});
            skLineSegment(sketch, "E11.63.5", {"start": v(50.73, 53.47) * mm, "end": v(50.88, 53.3) * mm});
            skArc(sketch, "E11.63.6", {"start": v(50.62, 53.98) * mm, "mid": v(50.6, 53.71) * mm, "end": v(50.73, 53.47) * mm});
            skArc(sketch, "E11.63.7", {"start": v(51.58, 56.28) * mm, "mid": v(51.06, 55.15) * mm, "end": v(50.62, 53.98) * mm});
            skLineSegment(sketch, "E11.63.8", {"start": v(51.58, 56.28) * mm, "end": v(52.95, 57.53) * mm});
            skArc(sketch, "E11.63.9", {"start": v(52.95, 57.53) * mm, "mid": v(53.11, 57.9) * mm, "end": v(52.94, 58.28) * mm});
            skArc(sketch, "E11.64.0", {"start": v(51, 59.99) * mm, "mid": v(50.63, 60.1) * mm, "end": v(50.29, 59.93) * mm});
            skLineSegment(sketch, "E11.64.1", {"start": v(48.98, 58.37) * mm, "end": v(50.29, 59.93) * mm});
            skArc(sketch, "E11.64.2", {"start": v(48.98, 58.37) * mm, "mid": v(47.87, 57.8) * mm, "end": v(46.72, 57.3) * mm});
            skArc(sketch, "E11.64.3", {"start": v(46.21, 57.4) * mm, "mid": v(46.45, 57.28) * mm, "end": v(46.72, 57.3) * mm});
            skLineSegment(sketch, "E11.64.4", {"start": v(46.21, 57.4) * mm, "end": v(46.04, 57.54) * mm});
            skLineSegment(sketch, "E11.64.5", {"start": v(45.87, 57.7) * mm, "end": v(46.04, 57.54) * mm});
            skArc(sketch, "E11.64.6", {"start": v(45.72, 58.19) * mm, "mid": v(45.73, 57.92) * mm, "end": v(45.87, 57.7) * mm});
            skArc(sketch, "E11.64.7", {"start": v(46.48, 60.56) * mm, "mid": v(46.06, 59.39) * mm, "end": v(45.72, 58.19) * mm});
            skLineSegment(sketch, "E11.64.8", {"start": v(46.48, 60.56) * mm, "end": v(47.73, 61.93) * mm});
            skArc(sketch, "E11.64.9", {"start": v(47.73, 61.93) * mm, "mid": v(47.86, 62.32) * mm, "end": v(47.66, 62.68) * mm});
            skArc(sketch, "E11.65.0", {"start": v(45.58, 64.2) * mm, "mid": v(45.2, 64.3) * mm, "end": v(44.87, 64.08) * mm});
            skLineSegment(sketch, "E11.65.1", {"start": v(43.7, 62.42) * mm, "end": v(44.87, 64.08) * mm});
            skArc(sketch, "E11.65.2", {"start": v(43.7, 62.42) * mm, "mid": v(42.65, 61.76) * mm, "end": v(41.55, 61.16) * mm});
            skArc(sketch, "E11.65.3", {"start": v(41.03, 61.2) * mm, "mid": v(41.29, 61.11) * mm, "end": v(41.55, 61.16) * mm});
            skLineSegment(sketch, "E11.65.4", {"start": v(41.03, 61.2) * mm, "end": v(40.85, 61.33) * mm});
            skLineSegment(sketch, "E11.65.5", {"start": v(40.67, 61.47) * mm, "end": v(40.85, 61.33) * mm});
            skArc(sketch, "E11.65.6", {"start": v(40.48, 61.95) * mm, "mid": v(40.5, 61.68) * mm, "end": v(40.67, 61.47) * mm});
            skArc(sketch, "E11.65.7", {"start": v(41.03, 64.39) * mm, "mid": v(40.71, 63.18) * mm, "end": v(40.48, 61.95) * mm});
            skLineSegment(sketch, "E11.65.8", {"start": v(41.03, 64.39) * mm, "end": v(42.15, 65.85) * mm});
            skArc(sketch, "E11.65.9", {"start": v(42.15, 65.85) * mm, "mid": v(42.25, 66.25) * mm, "end": v(42.02, 66.6) * mm});
            skArc(sketch, "E11.66.0", {"start": v(39.81, 67.93) * mm, "mid": v(39.43, 67.99) * mm, "end": v(39.12, 67.75) * mm});
            skLineSegment(sketch, "E11.66.1", {"start": v(38.1, 66) * mm, "end": v(39.12, 67.75) * mm});
            skArc(sketch, "E11.66.2", {"start": v(38.1, 66) * mm, "mid": v(37.1, 65.24) * mm, "end": v(36.06, 64.55) * mm});
            skArc(sketch, "E11.66.3", {"start": v(35.54, 64.55) * mm, "mid": v(35.8, 64.48) * mm, "end": v(36.06, 64.55) * mm});
            skLineSegment(sketch, "E11.66.4", {"start": v(35.54, 64.55) * mm, "end": v(35.35, 64.66) * mm});
            skLineSegment(sketch, "E11.66.5", {"start": v(35.16, 64.78) * mm, "end": v(35.35, 64.66) * mm});
            skArc(sketch, "E11.66.6", {"start": v(34.92, 65.24) * mm, "mid": v(34.98, 64.98) * mm, "end": v(35.16, 64.78) * mm});
            skArc(sketch, "E11.66.7", {"start": v(35.26, 67.72) * mm, "mid": v(35.05, 66.48) * mm, "end": v(34.92, 65.24) * mm});
            skLineSegment(sketch, "E11.66.8", {"start": v(35.26, 67.72) * mm, "end": v(36.25, 69.28) * mm});
            skArc(sketch, "E11.66.9", {"start": v(36.25, 69.28) * mm, "mid": v(36.31, 69.68) * mm, "end": v(36.06, 70) * mm});
            skArc(sketch, "E11.67.0", {"start": v(33.74, 71.15) * mm, "mid": v(33.35, 71.16) * mm, "end": v(33.06, 70.9) * mm});
            skLineSegment(sketch, "E11.67.1", {"start": v(32.2, 69.06) * mm, "end": v(33.06, 70.9) * mm});
            skArc(sketch, "E11.67.2", {"start": v(32.2, 69.06) * mm, "mid": v(31.28, 68.22) * mm, "end": v(30.3, 67.45) * mm});
            skArc(sketch, "E11.67.3", {"start": v(29.78, 67.4) * mm, "mid": v(30.05, 67.35) * mm, "end": v(30.3, 67.45) * mm});
            skLineSegment(sketch, "E11.67.4", {"start": v(29.78, 67.4) * mm, "end": v(29.58, 67.5) * mm});
            skLineSegment(sketch, "E11.67.5", {"start": v(29.38, 67.6) * mm, "end": v(29.58, 67.5) * mm});
            skArc(sketch, "E11.67.6", {"start": v(29.1, 68.04) * mm, "mid": v(29.18, 67.78) * mm, "end": v(29.38, 67.6) * mm});
            skArc(sketch, "E11.67.7", {"start": v(29.22, 70.53) * mm, "mid": v(29.12, 69.29) * mm, "end": v(29.1, 68.04) * mm});
            skLineSegment(sketch, "E11.67.8", {"start": v(29.22, 70.53) * mm, "end": v(30.08, 72.17) * mm});
            skArc(sketch, "E11.67.9", {"start": v(30.08, 72.17) * mm, "mid": v(30.1, 72.58) * mm, "end": v(29.82, 72.88) * mm});
            skArc(sketch, "E11.68.0", {"start": v(27.41, 73.81) * mm, "mid": v(27.02, 73.8) * mm, "end": v(26.76, 73.51) * mm});
            skLineSegment(sketch, "E11.68.1", {"start": v(26.06, 71.6) * mm, "end": v(26.76, 73.51) * mm});
            skArc(sketch, "E11.68.2", {"start": v(26.06, 71.6) * mm, "mid": v(25.21, 70.7) * mm, "end": v(24.3, 69.83) * mm});
            skArc(sketch, "E11.68.3", {"start": v(23.8, 69.74) * mm, "mid": v(24.06, 69.72) * mm, "end": v(24.3, 69.83) * mm});
            skLineSegment(sketch, "E11.68.4", {"start": v(23.8, 69.74) * mm, "end": v(23.58, 69.81) * mm});
            skLineSegment(sketch, "E11.68.5", {"start": v(23.37, 69.9) * mm, "end": v(23.58, 69.81) * mm});
            skArc(sketch, "E11.68.6", {"start": v(23.06, 70.32) * mm, "mid": v(23.16, 70.07) * mm, "end": v(23.37, 69.9) * mm});
            skArc(sketch, "E11.68.7", {"start": v(22.96, 72.8) * mm, "mid": v(22.97, 71.56) * mm, "end": v(23.06, 70.32) * mm});
            skLineSegment(sketch, "E11.68.8", {"start": v(22.96, 72.8) * mm, "end": v(23.67, 74.52) * mm});
            skArc(sketch, "E11.68.9", {"start": v(23.67, 74.52) * mm, "mid": v(23.66, 74.93) * mm, "end": v(23.35, 75.2) * mm});
            skArc(sketch, "E11.69.0", {"start": v(20.87, 75.92) * mm, "mid": v(20.49, 75.87) * mm, "end": v(20.25, 75.56) * mm});
            skLineSegment(sketch, "E11.69.1", {"start": v(19.72, 73.6) * mm, "end": v(20.25, 75.56) * mm});
            skArc(sketch, "E11.69.2", {"start": v(19.72, 73.6) * mm, "mid": v(18.95, 72.62) * mm, "end": v(18.12, 71.69) * mm});
            skArc(sketch, "E11.69.3", {"start": v(17.63, 71.55) * mm, "mid": v(17.9, 71.55) * mm, "end": v(18.12, 71.69) * mm});
            skLineSegment(sketch, "E11.69.4", {"start": v(17.63, 71.55) * mm, "end": v(17.4, 71.6) * mm});
            skLineSegment(sketch, "E11.69.5", {"start": v(17.2, 71.67) * mm, "end": v(17.4, 71.6) * mm});
            skArc(sketch, "E11.69.6", {"start": v(16.85, 72.06) * mm, "mid": v(16.97, 71.82) * mm, "end": v(17.2, 71.67) * mm});
            skArc(sketch, "E11.69.7", {"start": v(16.53, 74.53) * mm, "mid": v(16.65, 73.3) * mm, "end": v(16.85, 72.06) * mm});
            skLineSegment(sketch, "E11.69.8", {"start": v(16.53, 74.53) * mm, "end": v(17.09, 76.3) * mm});
            skArc(sketch, "E11.69.9", {"start": v(17.09, 76.3) * mm, "mid": v(17.04, 76.7) * mm, "end": v(16.7, 76.95) * mm});
            skArc(sketch, "E11.70.0", {"start": v(14.18, 77.45) * mm, "mid": v(13.8, 77.37) * mm, "end": v(13.58, 77.04) * mm});
            skLineSegment(sketch, "E11.70.1", {"start": v(13.23, 75.04) * mm, "end": v(13.58, 77.04) * mm});
            skArc(sketch, "E11.70.2", {"start": v(13.23, 75.04) * mm, "mid": v(12.55, 74) * mm, "end": v(11.8, 73) * mm});
            skArc(sketch, "E11.70.3", {"start": v(11.32, 72.8) * mm, "mid": v(11.6, 72.83) * mm, "end": v(11.8, 73) * mm});
            skLineSegment(sketch, "E11.70.4", {"start": v(11.32, 72.8) * mm, "end": v(11.1, 72.85) * mm});
            skLineSegment(sketch, "E11.70.5", {"start": v(10.88, 72.9) * mm, "end": v(11.1, 72.85) * mm});
            skArc(sketch, "E11.70.6", {"start": v(10.5, 73.25) * mm, "mid": v(10.64, 73.02) * mm, "end": v(10.88, 72.9) * mm});
            skArc(sketch, "E11.70.7", {"start": v(9.97, 75.7) * mm, "mid": v(10.2, 74.46) * mm, "end": v(10.5, 73.25) * mm});
            skLineSegment(sketch, "E11.70.8", {"start": v(9.97, 75.7) * mm, "end": v(10.37, 77.5) * mm});
            skArc(sketch, "E11.70.9", {"start": v(10.37, 77.5) * mm, "mid": v(10.3, 77.9) * mm, "end": v(9.94, 78.11) * mm});
            skArc(sketch, "E11.71.0", {"start": v(7.37, 78.4) * mm, "mid": v(7, 78.28) * mm, "end": v(6.82, 77.93) * mm});
            skLineSegment(sketch, "E11.71.1", {"start": v(6.64, 75.91) * mm, "end": v(6.82, 77.93) * mm});
            skArc(sketch, "E11.71.2", {"start": v(6.64, 75.91) * mm, "mid": v(6.06, 74.8) * mm, "end": v(5.4, 73.74) * mm});
            skArc(sketch, "E11.71.3", {"start": v(4.93, 73.52) * mm, "mid": v(5.2, 73.57) * mm, "end": v(5.4, 73.74) * mm});
            skLineSegment(sketch, "E11.71.4", {"start": v(4.93, 73.52) * mm, "end": v(4.7, 73.54) * mm});
            skLineSegment(sketch, "E11.71.5", {"start": v(4.49, 73.57) * mm, "end": v(4.7, 73.54) * mm});
            skArc(sketch, "E11.71.6", {"start": v(4.08, 73.89) * mm, "mid": v(4.24, 73.67) * mm, "end": v(4.49, 73.57) * mm});
            skArc(sketch, "E11.71.7", {"start": v(3.34, 76.27) * mm, "mid": v(3.67, 75.07) * mm, "end": v(4.08, 73.89) * mm});
            skLineSegment(sketch, "E11.71.8", {"start": v(3.34, 76.27) * mm, "end": v(3.58, 78.1) * mm});
            skArc(sketch, "E11.71.9", {"start": v(3.58, 78.1) * mm, "mid": v(3.46, 78.5) * mm, "end": v(3.1, 78.68) * mm});
            skArc(sketch, "E12.trimOffspring", {"start": v(-10.62, 78.02) * mm, "mid": v(-11.9, 77.84) * mm, "end": v(-13.17, 77.63) * mm});
            skArc(sketch, "E13.trimOffspring", {"start": v(-17.37, 76.8) * mm, "mid": v(-18.63, 76.5) * mm, "end": v(-19.89, 76.19) * mm});
            skArc(sketch, "E14.trimOffspring", {"start": v(-24, 75) * mm, "mid": v(-25.23, 74.59) * mm, "end": v(-26.45, 74.16) * mm});
            skArc(sketch, "E15.trimOffspring", {"start": v(-30.45, 72.62) * mm, "mid": v(-31.63, 72.1) * mm, "end": v(-32.81, 71.58) * mm});
            skArc(sketch, "E16.trimOffspring", {"start": v(-36.66, 69.69) * mm, "mid": v(-37.8, 69.07) * mm, "end": v(-38.93, 68.45) * mm});
            skArc(sketch, "E17.trimOffspring", {"start": v(-42.6, 66.22) * mm, "mid": v(-43.67, 65.52) * mm, "end": v(-44.74, 64.8) * mm});
            skArc(sketch, "E18.trimOffspring", {"start": v(-48.2, 62.26) * mm, "mid": v(-49.22, 61.46) * mm, "end": v(-50.22, 60.65) * mm});
            skArc(sketch, "E19.trimOffspring", {"start": v(-53.45, 57.82) * mm, "mid": v(-54.39, 56.94) * mm, "end": v(-55.31, 56.04) * mm});
            skArc(sketch, "E20.trimOffspring", {"start": v(-58.28, 52.94) * mm, "mid": v(-59.14, 51.98) * mm, "end": v(-59.99, 51) * mm});
            skArc(sketch, "E21.trimOffspring", {"start": v(3.1, 78.68) * mm, "mid": v(1.8, 78.72) * mm, "end": v(0.51, 78.74) * mm});
            skArc(sketch, "E22.trimOffspring", {"start": v(9.94, 78.11) * mm, "mid": v(8.66, 78.26) * mm, "end": v(7.37, 78.4) * mm});
            skArc(sketch, "E23.trimOffspring", {"start": v(16.7, 76.95) * mm, "mid": v(15.45, 77.21) * mm, "end": v(14.18, 77.45) * mm});
            skArc(sketch, "E24.trimOffspring", {"start": v(23.35, 75.2) * mm, "mid": v(22.12, 75.57) * mm, "end": v(20.87, 75.92) * mm});
            skArc(sketch, "E25.trimOffspring", {"start": v(29.82, 72.88) * mm, "mid": v(28.62, 73.36) * mm, "end": v(27.41, 73.81) * mm});
            skArc(sketch, "E26.trimOffspring", {"start": v(36.06, 70) * mm, "mid": v(34.9, 70.58) * mm, "end": v(33.74, 71.15) * mm});
            skArc(sketch, "E27.trimOffspring", {"start": v(42.02, 66.6) * mm, "mid": v(40.92, 67.27) * mm, "end": v(39.81, 67.93) * mm});
            skArc(sketch, "E28.trimOffspring", {"start": v(47.66, 62.68) * mm, "mid": v(46.63, 63.45) * mm, "end": v(45.58, 64.2) * mm});
            skArc(sketch, "E29.trimOffspring", {"start": v(52.94, 58.28) * mm, "mid": v(51.98, 59.14) * mm, "end": v(51, 59.99) * mm});
            skArc(sketch, "E30.trimOffspring", {"start": v(57.82, 53.45) * mm, "mid": v(56.94, 54.39) * mm, "end": v(56.04, 55.31) * mm});
            skArc(sketch, "E31.trimOffspring", {"start": v(62.26, 48.2) * mm, "mid": v(61.46, 49.22) * mm, "end": v(60.65, 50.22) * mm});
            skArc(sketch, "E32.trimOffspring", {"start": v(66.22, 42.6) * mm, "mid": v(65.52, 43.67) * mm, "end": v(64.8, 44.74) * mm});
            skArc(sketch, "E33.trimOffspring", {"start": v(69.69, 36.66) * mm, "mid": v(69.07, 37.8) * mm, "end": v(68.45, 38.93) * mm});
            skArc(sketch, "E34.trimOffspring", {"start": v(72.62, 30.45) * mm, "mid": v(72.1, 31.63) * mm, "end": v(71.58, 32.81) * mm});
            skArc(sketch, "E35.trimOffspring", {"start": v(75, 24) * mm, "mid": v(74.59, 25.23) * mm, "end": v(74.16, 26.45) * mm});
            skArc(sketch, "E36.trimOffspring", {"start": v(76.8, 17.37) * mm, "mid": v(76.5, 18.63) * mm, "end": v(76.19, 19.89) * mm});
            skArc(sketch, "E37.trimOffspring", {"start": v(78.02, 10.62) * mm, "mid": v(77.84, 11.9) * mm, "end": v(77.63, 13.17) * mm});
            skArc(sketch, "E38.trimOffspring", {"start": v(78.65, 3.78) * mm, "mid": v(78.58, 5.06) * mm, "end": v(78.48, 6.35) * mm});
            skArc(sketch, "E39.trimOffspring", {"start": v(78.68, -3.1) * mm, "mid": v(78.72, -1.8) * mm, "end": v(78.74, -0.51) * mm});
            skArc(sketch, "E40.trimOffspring", {"start": v(78.11, -9.94) * mm, "mid": v(78.26, -8.66) * mm, "end": v(78.4, -7.37) * mm});
            skArc(sketch, "E41.trimOffspring", {"start": v(76.95, -16.7) * mm, "mid": v(77.21, -15.45) * mm, "end": v(77.45, -14.18) * mm});
            skArc(sketch, "E42.trimOffspring", {"start": v(72.88, -29.82) * mm, "mid": v(73.36, -28.62) * mm, "end": v(73.81, -27.41) * mm});
            skArc(sketch, "E43.trimOffspring", {"start": v(70, -36.06) * mm, "mid": v(70.58, -34.9) * mm, "end": v(71.15, -33.74) * mm});
            skArc(sketch, "E44.trimOffspring", {"start": v(66.6, -42.02) * mm, "mid": v(67.27, -40.92) * mm, "end": v(67.93, -39.81) * mm});
            skArc(sketch, "E45.trimOffspring", {"start": v(62.68, -47.66) * mm, "mid": v(63.45, -46.63) * mm, "end": v(64.2, -45.58) * mm});
            skArc(sketch, "E46.trimOffspring", {"start": v(58.28, -52.94) * mm, "mid": v(59.14, -51.98) * mm, "end": v(59.99, -51) * mm});
            skArc(sketch, "E47.trimOffspring", {"start": v(53.45, -57.82) * mm, "mid": v(54.39, -56.94) * mm, "end": v(55.31, -56.04) * mm});
            skArc(sketch, "E48.trimOffspring", {"start": v(48.2, -62.26) * mm, "mid": v(49.22, -61.46) * mm, "end": v(50.22, -60.65) * mm});
            skArc(sketch, "E49.trimOffspring", {"start": v(42.6, -66.22) * mm, "mid": v(43.67, -65.52) * mm, "end": v(44.74, -64.8) * mm});
            skArc(sketch, "E50.trimOffspring", {"start": v(36.66, -69.69) * mm, "mid": v(37.8, -69.07) * mm, "end": v(38.93, -68.45) * mm});
            skArc(sketch, "E51.trimOffspring", {"start": v(30.45, -72.62) * mm, "mid": v(31.63, -72.1) * mm, "end": v(32.81, -71.58) * mm});
            skArc(sketch, "E52.trimOffspring", {"start": v(24, -75) * mm, "mid": v(25.23, -74.59) * mm, "end": v(26.45, -74.16) * mm});
            skArc(sketch, "E53.trimOffspring", {"start": v(17.37, -76.8) * mm, "mid": v(18.63, -76.5) * mm, "end": v(19.89, -76.19) * mm});
            skArc(sketch, "E54.trimOffspring", {"start": v(10.62, -78.02) * mm, "mid": v(11.9, -77.84) * mm, "end": v(13.17, -77.63) * mm});
            skArc(sketch, "E55.trimOffspring", {"start": v(3.78, -78.65) * mm, "mid": v(5.06, -78.58) * mm, "end": v(6.35, -78.48) * mm});
            skArc(sketch, "E56.trimOffspring", {"start": v(-3.1, -78.68) * mm, "mid": v(-1.8, -78.72) * mm, "end": v(-0.51, -78.74) * mm});
            skArc(sketch, "E57.trimOffspring", {"start": v(-9.94, -78.11) * mm, "mid": v(-8.66, -78.26) * mm, "end": v(-7.37, -78.4) * mm});
            skArc(sketch, "E58.trimOffspring", {"start": v(-16.7, -76.95) * mm, "mid": v(-15.45, -77.21) * mm, "end": v(-14.18, -77.45) * mm});
            skArc(sketch, "E59.trimOffspring", {"start": v(-23.35, -75.2) * mm, "mid": v(-22.12, -75.57) * mm, "end": v(-20.87, -75.92) * mm});
            skArc(sketch, "E60.trimOffspring", {"start": v(-29.82, -72.88) * mm, "mid": v(-28.62, -73.36) * mm, "end": v(-27.41, -73.81) * mm});
            skArc(sketch, "E61.trimOffspring", {"start": v(-36.06, -70) * mm, "mid": v(-34.9, -70.58) * mm, "end": v(-33.74, -71.15) * mm});
            skArc(sketch, "E62.trimOffspring", {"start": v(-42.02, -66.6) * mm, "mid": v(-40.92, -67.27) * mm, "end": v(-39.81, -67.93) * mm});
            skArc(sketch, "E63.trimOffspring", {"start": v(-47.66, -62.68) * mm, "mid": v(-46.63, -63.45) * mm, "end": v(-45.58, -64.2) * mm});
            skArc(sketch, "E64.trimOffspring", {"start": v(-52.94, -58.28) * mm, "mid": v(-51.98, -59.14) * mm, "end": v(-51, -59.99) * mm});
            skArc(sketch, "E65.trimOffspring", {"start": v(-57.82, -53.45) * mm, "mid": v(-56.94, -54.39) * mm, "end": v(-56.04, -55.31) * mm});
            skArc(sketch, "E66.trimOffspring", {"start": v(-62.26, -48.2) * mm, "mid": v(-61.46, -49.22) * mm, "end": v(-60.65, -50.22) * mm});
            skArc(sketch, "E67.trimOffspring", {"start": v(-66.22, -42.6) * mm, "mid": v(-65.52, -43.67) * mm, "end": v(-64.8, -44.74) * mm});
            skArc(sketch, "E68.trimOffspring", {"start": v(-69.69, -36.66) * mm, "mid": v(-69.07, -37.8) * mm, "end": v(-68.45, -38.93) * mm});
            skArc(sketch, "E69.trimOffspring", {"start": v(-72.62, -30.45) * mm, "mid": v(-72.1, -31.63) * mm, "end": v(-71.58, -32.81) * mm});
            skArc(sketch, "E70.trimOffspring", {"start": v(-75, -24) * mm, "mid": v(-74.59, -25.23) * mm, "end": v(-74.16, -26.45) * mm});
            skArc(sketch, "E71.trimOffspring", {"start": v(-76.8, -17.37) * mm, "mid": v(-76.5, -18.63) * mm, "end": v(-76.19, -19.89) * mm});
            skArc(sketch, "E72.trimOffspring", {"start": v(-78.02, -10.62) * mm, "mid": v(-77.84, -11.9) * mm, "end": v(-77.63, -13.17) * mm});
            skArc(sketch, "E73.trimOffspring", {"start": v(-78.65, -3.78) * mm, "mid": v(-78.58, -5.06) * mm, "end": v(-78.48, -6.35) * mm});
            skArc(sketch, "E74.trimOffspring", {"start": v(-78.68, 3.1) * mm, "mid": v(-78.72, 1.8) * mm, "end": v(-78.74, 0.51) * mm});
            skArc(sketch, "E75.trimOffspring", {"start": v(-78.11, 9.94) * mm, "mid": v(-78.26, 8.66) * mm, "end": v(-78.4, 7.37) * mm});
            skArc(sketch, "E76.trimOffspring", {"start": v(-76.95, 16.7) * mm, "mid": v(-77.21, 15.45) * mm, "end": v(-77.45, 14.18) * mm});
            skArc(sketch, "E77.trimOffspring", {"start": v(-75.2, 23.35) * mm, "mid": v(-75.57, 22.12) * mm, "end": v(-75.92, 20.87) * mm});
            skArc(sketch, "E78.trimOffspring", {"start": v(-72.88, 29.82) * mm, "mid": v(-73.36, 28.62) * mm, "end": v(-73.81, 27.41) * mm});
            skArc(sketch, "E79.trimOffspring", {"start": v(-70, 36.06) * mm, "mid": v(-70.58, 34.9) * mm, "end": v(-71.15, 33.74) * mm});
            skArc(sketch, "E80.trimOffspring", {"start": v(-66.6, 42.02) * mm, "mid": v(-67.27, 40.92) * mm, "end": v(-67.93, 39.81) * mm});
            skArc(sketch, "E81.trimOffspring", {"start": v(-62.68, 47.66) * mm, "mid": v(-63.45, 46.63) * mm, "end": v(-64.2, 45.58) * mm});
            skLineSegment(sketch, "E82", {"start": v(75.2, -23.35) * mm, "end": v(75.92, -20.87) * mm});
            skCircle(sketch, "E83", {"center": v(0, 0) * mm, "radius": 82.55 * mm});
            skSolve(sketch);
        }
        {
            var Q0;
            Q0 = qSketchRegion(id + "F0", true);
            extrude(context, id + "F1", {"entities" : qUnion([Q0]), "depth" : 25.4 * mm});
        }
        {
            var Q0;
            Q0=makeQuery(id+"F1.opExtrude","CAP_FACE",FACE,{"disambiguationData":[OSD([sQuery(id+"F0.wireOp",EDGE,"E0"),sQuery(id+"F0.wireOp",EDGE,"E1.MirrorCS"),sQuery(id+"F0.wireOp",EDGE,"E2.MirrorCS"),sQuery(id+"F0.wireOp",EDGE,"E3.MirrorCS"),sQuery(id+"F0.wireOp",EDGE,"E4.MirrorCS"),sQuery(id+"F0.wireOp",EDGE,"E5.MirrorCS"),sQuery(id+"F0.wireOp",EDGE,"E6.MirrorCS"),sQuery(id+"F0.wireOp",EDGE,"E7.filletArc"),sQuery(id+"F0.wireOp",EDGE,"E8.filletArc"),sQuery(id+"F0.wireOp",EDGE,"E9.filletArc"),sQuery(id+"F0.wireOp",EDGE,"E10.filletArc"),sQuery(id+"F0.wireOp",EDGE,"E11.1.0"),sQuery(id+"F0.wireOp",EDGE,"E11.1.1"),sQuery(id+"F0.wireOp",EDGE,"E11.1.2"),sQuery(id+"F0.wireOp",EDGE,"E11.1.3"),sQuery(id+"F0.wireOp",EDGE,"E11.1.4"),sQuery(id+"F0.wireOp",EDGE,"E11.1.5"),sQuery(id+"F0.wireOp",EDGE,"E11.1.6"),sQuery(id+"F0.wireOp",EDGE,"E11.1.7"),sQuery(id+"F0.wireOp",EDGE,"E11.1.8"),sQuery(id+"F0.wireOp",EDGE,"E11.1.9"),sQuery(id+"F0.wireOp",EDGE,"E11.2.0"),sQuery(id+"F0.wireOp",EDGE,"E11.2.1"),sQuery(id+"F0.wireOp",EDGE,"E11.2.2"),sQuery(id+"F0.wireOp",EDGE,"E11.2.3"),sQuery(id+"F0.wireOp",EDGE,"E11.2.4"),sQuery(id+"F0.wireOp",EDGE,"E11.2.5"),sQuery(id+"F0.wireOp",EDGE,"E11.2.6"),sQuery(id+"F0.wireOp",EDGE,"E11.2.7"),sQuery(id+"F0.wireOp",EDGE,"E11.2.8"),sQuery(id+"F0.wireOp",EDGE,"E11.2.9"),sQuery(id+"F0.wireOp",EDGE,"E11.3.0"),sQuery(id+"F0.wireOp",EDGE,"E11.3.1"),sQuery(id+"F0.wireOp",EDGE,"E11.3.2"),sQuery(id+"F0.wireOp",EDGE,"E11.3.3"),sQuery(id+"F0.wireOp",EDGE,"E11.3.4"),sQuery(id+"F0.wireOp",EDGE,"E11.3.5"),sQuery(id+"F0.wireOp",EDGE,"E11.3.6"),sQuery(id+"F0.wireOp",EDGE,"E11.3.7"),sQuery(id+"F0.wireOp",EDGE,"E11.3.8"),sQuery(id+"F0.wireOp",EDGE,"E11.3.9"),sQuery(id+"F0.wireOp",EDGE,"E11.4.0"),sQuery(id+"F0.wireOp",EDGE,"E11.4.1"),sQuery(id+"F0.wireOp",EDGE,"E11.4.2"),sQuery(id+"F0.wireOp",EDGE,"E11.4.3"),sQuery(id+"F0.wireOp",EDGE,"E11.4.4"),sQuery(id+"F0.wireOp",EDGE,"E11.4.5"),sQuery(id+"F0.wireOp",EDGE,"E11.4.6"),sQuery(id+"F0.wireOp",EDGE,"E11.4.7"),sQuery(id+"F0.wireOp",EDGE,"E11.4.8"),sQuery(id+"F0.wireOp",EDGE,"E11.4.9"),sQuery(id+"F0.wireOp",EDGE,"E11.5.0"),sQuery(id+"F0.wireOp",EDGE,"E11.5.1"),sQuery(id+"F0.wireOp",EDGE,"E11.5.2"),sQuery(id+"F0.wireOp",EDGE,"E11.5.3"),sQuery(id+"F0.wireOp",EDGE,"E11.5.4"),sQuery(id+"F0.wireOp",EDGE,"E11.5.5"),sQuery(id+"F0.wireOp",EDGE,"E11.5.6"),sQuery(id+"F0.wireOp",EDGE,"E11.5.7"),sQuery(id+"F0.wireOp",EDGE,"E11.5.8"),sQuery(id+"F0.wireOp",EDGE,"E11.5.9"),sQuery(id+"F0.wireOp",EDGE,"E11.6.0"),sQuery(id+"F0.wireOp",EDGE,"E11.6.1"),sQuery(id+"F0.wireOp",EDGE,"E11.6.2"),sQuery(id+"F0.wireOp",EDGE,"E11.6.3"),sQuery(id+"F0.wireOp",EDGE,"E11.6.4"),sQuery(id+"F0.wireOp",EDGE,"E11.6.5"),sQuery(id+"F0.wireOp",EDGE,"E11.6.6"),sQuery(id+"F0.wireOp",EDGE,"E11.6.7"),sQuery(id+"F0.wireOp",EDGE,"E11.6.8"),sQuery(id+"F0.wireOp",EDGE,"E11.6.9"),sQuery(id+"F0.wireOp",EDGE,"E11.7.0"),sQuery(id+"F0.wireOp",EDGE,"E11.7.1"),sQuery(id+"F0.wireOp",EDGE,"E11.7.2"),sQuery(id+"F0.wireOp",EDGE,"E11.7.3"),sQuery(id+"F0.wireOp",EDGE,"E11.7.4"),sQuery(id+"F0.wireOp",EDGE,"E11.7.5"),sQuery(id+"F0.wireOp",EDGE,"E11.7.6"),sQuery(id+"F0.wireOp",EDGE,"E11.7.7"),sQuery(id+"F0.wireOp",EDGE,"E11.7.8"),sQuery(id+"F0.wireOp",EDGE,"E11.7.9"),sQuery(id+"F0.wireOp",EDGE,"E11.8.0"),sQuery(id+"F0.wireOp",EDGE,"E11.8.1"),sQuery(id+"F0.wireOp",EDGE,"E11.8.2"),sQuery(id+"F0.wireOp",EDGE,"E11.8.3"),sQuery(id+"F0.wireOp",EDGE,"E11.8.4"),sQuery(id+"F0.wireOp",EDGE,"E11.8.5"),sQuery(id+"F0.wireOp",EDGE,"E11.8.6"),sQuery(id+"F0.wireOp",EDGE,"E11.8.7"),sQuery(id+"F0.wireOp",EDGE,"E11.8.8"),sQuery(id+"F0.wireOp",EDGE,"E11.8.9"),sQuery(id+"F0.wireOp",EDGE,"E11.9.0"),sQuery(id+"F0.wireOp",EDGE,"E11.9.1"),sQuery(id+"F0.wireOp",EDGE,"E11.9.2"),sQuery(id+"F0.wireOp",EDGE,"E11.9.3"),sQuery(id+"F0.wireOp",EDGE,"E11.9.4"),sQuery(id+"F0.wireOp",EDGE,"E11.9.5"),sQuery(id+"F0.wireOp",EDGE,"E11.9.6"),sQuery(id+"F0.wireOp",EDGE,"E11.9.7"),sQuery(id+"F0.wireOp",EDGE,"E11.9.8"),sQuery(id+"F0.wireOp",EDGE,"E11.9.9"),sQuery(id+"F0.wireOp",EDGE,"E11.10.0"),sQuery(id+"F0.wireOp",EDGE,"E11.10.1"),sQuery(id+"F0.wireOp",EDGE,"E11.10.2"),sQuery(id+"F0.wireOp",EDGE,"E11.10.3"),sQuery(id+"F0.wireOp",EDGE,"E11.10.4"),sQuery(id+"F0.wireOp",EDGE,"E11.10.5"),sQuery(id+"F0.wireOp",EDGE,"E11.10.6"),sQuery(id+"F0.wireOp",EDGE,"E11.10.7"),sQuery(id+"F0.wireOp",EDGE,"E11.10.8"),sQuery(id+"F0.wireOp",EDGE,"E11.10.9"),sQuery(id+"F0.wireOp",EDGE,"E11.11.0"),sQuery(id+"F0.wireOp",EDGE,"E11.11.1"),sQuery(id+"F0.wireOp",EDGE,"E11.11.2"),sQuery(id+"F0.wireOp",EDGE,"E11.11.3"),sQuery(id+"F0.wireOp",EDGE,"E11.11.4"),sQuery(id+"F0.wireOp",EDGE,"E11.11.5"),sQuery(id+"F0.wireOp",EDGE,"E11.11.6"),sQuery(id+"F0.wireOp",EDGE,"E11.11.7"),sQuery(id+"F0.wireOp",EDGE,"E11.11.8"),sQuery(id+"F0.wireOp",EDGE,"E11.11.9"),sQuery(id+"F0.wireOp",EDGE,"E11.12.0"),sQuery(id+"F0.wireOp",EDGE,"E11.12.1"),sQuery(id+"F0.wireOp",EDGE,"E11.12.2"),sQuery(id+"F0.wireOp",EDGE,"E11.12.3"),sQuery(id+"F0.wireOp",EDGE,"E11.12.4"),sQuery(id+"F0.wireOp",EDGE,"E11.12.5"),sQuery(id+"F0.wireOp",EDGE,"E11.12.6"),sQuery(id+"F0.wireOp",EDGE,"E11.12.7"),sQuery(id+"F0.wireOp",EDGE,"E11.12.8"),sQuery(id+"F0.wireOp",EDGE,"E11.12.9"),sQuery(id+"F0.wireOp",EDGE,"E11.13.0"),sQuery(id+"F0.wireOp",EDGE,"E11.13.1"),sQuery(id+"F0.wireOp",EDGE,"E11.13.2"),sQuery(id+"F0.wireOp",EDGE,"E11.13.3"),sQuery(id+"F0.wireOp",EDGE,"E11.13.4"),sQuery(id+"F0.wireOp",EDGE,"E11.13.5"),sQuery(id+"F0.wireOp",EDGE,"E11.13.6"),sQuery(id+"F0.wireOp",EDGE,"E11.13.7"),sQuery(id+"F0.wireOp",EDGE,"E11.13.8"),sQuery(id+"F0.wireOp",EDGE,"E11.13.9"),sQuery(id+"F0.wireOp",EDGE,"E11.14.0"),sQuery(id+"F0.wireOp",EDGE,"E11.14.1"),sQuery(id+"F0.wireOp",EDGE,"E11.14.2"),sQuery(id+"F0.wireOp",EDGE,"E11.14.3"),sQuery(id+"F0.wireOp",EDGE,"E11.14.4"),sQuery(id+"F0.wireOp",EDGE,"E11.14.5"),sQuery(id+"F0.wireOp",EDGE,"E11.14.6"),sQuery(id+"F0.wireOp",EDGE,"E11.14.7"),sQuery(id+"F0.wireOp",EDGE,"E11.14.8"),sQuery(id+"F0.wireOp",EDGE,"E11.14.9"),sQuery(id+"F0.wireOp",EDGE,"E11.15.0"),sQuery(id+"F0.wireOp",EDGE,"E11.15.1"),sQuery(id+"F0.wireOp",EDGE,"E11.15.2"),sQuery(id+"F0.wireOp",EDGE,"E11.15.3"),sQuery(id+"F0.wireOp",EDGE,"E11.15.4"),sQuery(id+"F0.wireOp",EDGE,"E11.15.5"),sQuery(id+"F0.wireOp",EDGE,"E11.15.6"),sQuery(id+"F0.wireOp",EDGE,"E11.15.7"),sQuery(id+"F0.wireOp",EDGE,"E11.15.8"),sQuery(id+"F0.wireOp",EDGE,"E11.15.9"),sQuery(id+"F0.wireOp",EDGE,"E11.16.0"),sQuery(id+"F0.wireOp",EDGE,"E11.16.1"),sQuery(id+"F0.wireOp",EDGE,"E11.16.2"),sQuery(id+"F0.wireOp",EDGE,"E11.16.3"),sQuery(id+"F0.wireOp",EDGE,"E11.16.4"),sQuery(id+"F0.wireOp",EDGE,"E11.16.5"),sQuery(id+"F0.wireOp",EDGE,"E11.16.6"),sQuery(id+"F0.wireOp",EDGE,"E11.16.7"),sQuery(id+"F0.wireOp",EDGE,"E11.16.8"),sQuery(id+"F0.wireOp",EDGE,"E11.16.9"),sQuery(id+"F0.wireOp",EDGE,"E11.17.0"),sQuery(id+"F0.wireOp",EDGE,"E11.17.1"),sQuery(id+"F0.wireOp",EDGE,"E11.17.2"),sQuery(id+"F0.wireOp",EDGE,"E11.17.3"),sQuery(id+"F0.wireOp",EDGE,"E11.17.4"),sQuery(id+"F0.wireOp",EDGE,"E11.17.5"),sQuery(id+"F0.wireOp",EDGE,"E11.17.6"),sQuery(id+"F0.wireOp",EDGE,"E11.17.7"),sQuery(id+"F0.wireOp",EDGE,"E11.17.8"),sQuery(id+"F0.wireOp",EDGE,"E11.17.9"),sQuery(id+"F0.wireOp",EDGE,"E11.18.0"),sQuery(id+"F0.wireOp",EDGE,"E11.18.1"),sQuery(id+"F0.wireOp",EDGE,"E11.18.2"),sQuery(id+"F0.wireOp",EDGE,"E11.18.3"),sQuery(id+"F0.wireOp",EDGE,"E11.18.4"),sQuery(id+"F0.wireOp",EDGE,"E11.18.5"),sQuery(id+"F0.wireOp",EDGE,"E11.18.6"),sQuery(id+"F0.wireOp",EDGE,"E11.18.7"),sQuery(id+"F0.wireOp",EDGE,"E11.18.8"),sQuery(id+"F0.wireOp",EDGE,"E11.18.9"),sQuery(id+"F0.wireOp",EDGE,"E11.19.0"),sQuery(id+"F0.wireOp",EDGE,"E11.19.1"),sQuery(id+"F0.wireOp",EDGE,"E11.19.2"),sQuery(id+"F0.wireOp",EDGE,"E11.19.3"),sQuery(id+"F0.wireOp",EDGE,"E11.19.4"),sQuery(id+"F0.wireOp",EDGE,"E11.19.5"),sQuery(id+"F0.wireOp",EDGE,"E11.19.6"),sQuery(id+"F0.wireOp",EDGE,"E11.19.7"),sQuery(id+"F0.wireOp",EDGE,"E11.19.8"),sQuery(id+"F0.wireOp",EDGE,"E11.19.9"),sQuery(id+"F0.wireOp",EDGE,"E11.20.0"),sQuery(id+"F0.wireOp",EDGE,"E11.20.1"),sQuery(id+"F0.wireOp",EDGE,"E11.20.2"),sQuery(id+"F0.wireOp",EDGE,"E11.20.3"),sQuery(id+"F0.wireOp",EDGE,"E11.20.4"),sQuery(id+"F0.wireOp",EDGE,"E11.20.5"),sQuery(id+"F0.wireOp",EDGE,"E11.20.6"),sQuery(id+"F0.wireOp",EDGE,"E11.20.7"),sQuery(id+"F0.wireOp",EDGE,"E11.20.8"),sQuery(id+"F0.wireOp",EDGE,"E11.20.9"),sQuery(id+"F0.wireOp",EDGE,"E11.21.0"),sQuery(id+"F0.wireOp",EDGE,"E11.21.1"),sQuery(id+"F0.wireOp",EDGE,"E11.21.2"),sQuery(id+"F0.wireOp",EDGE,"E11.21.3"),sQuery(id+"F0.wireOp",EDGE,"E11.21.4"),sQuery(id+"F0.wireOp",EDGE,"E11.21.5"),sQuery(id+"F0.wireOp",EDGE,"E11.21.6"),sQuery(id+"F0.wireOp",EDGE,"E11.21.7"),sQuery(id+"F0.wireOp",EDGE,"E11.21.8"),sQuery(id+"F0.wireOp",EDGE,"E11.21.9"),sQuery(id+"F0.wireOp",EDGE,"E11.22.0"),sQuery(id+"F0.wireOp",EDGE,"E11.22.1"),sQuery(id+"F0.wireOp",EDGE,"E11.22.2"),sQuery(id+"F0.wireOp",EDGE,"E11.22.3"),sQuery(id+"F0.wireOp",EDGE,"E11.22.4"),sQuery(id+"F0.wireOp",EDGE,"E11.22.5"),sQuery(id+"F0.wireOp",EDGE,"E11.22.6"),sQuery(id+"F0.wireOp",EDGE,"E11.22.7"),sQuery(id+"F0.wireOp",EDGE,"E11.22.8"),sQuery(id+"F0.wireOp",EDGE,"E11.22.9"),sQuery(id+"F0.wireOp",EDGE,"E11.23.0"),sQuery(id+"F0.wireOp",EDGE,"E11.23.1"),sQuery(id+"F0.wireOp",EDGE,"E11.23.2"),sQuery(id+"F0.wireOp",EDGE,"E11.23.3"),sQuery(id+"F0.wireOp",EDGE,"E11.23.4"),sQuery(id+"F0.wireOp",EDGE,"E11.23.5"),sQuery(id+"F0.wireOp",EDGE,"E11.23.6"),sQuery(id+"F0.wireOp",EDGE,"E11.23.7"),sQuery(id+"F0.wireOp",EDGE,"E11.23.8"),sQuery(id+"F0.wireOp",EDGE,"E11.23.9"),sQuery(id+"F0.wireOp",EDGE,"E11.24.0"),sQuery(id+"F0.wireOp",EDGE,"E11.24.1"),sQuery(id+"F0.wireOp",EDGE,"E11.24.2"),sQuery(id+"F0.wireOp",EDGE,"E11.24.3"),sQuery(id+"F0.wireOp",EDGE,"E11.24.4"),sQuery(id+"F0.wireOp",EDGE,"E11.24.5"),sQuery(id+"F0.wireOp",EDGE,"E11.24.6"),sQuery(id+"F0.wireOp",EDGE,"E11.24.7"),sQuery(id+"F0.wireOp",EDGE,"E11.24.8"),sQuery(id+"F0.wireOp",EDGE,"E11.24.9"),sQuery(id+"F0.wireOp",EDGE,"E11.25.0"),sQuery(id+"F0.wireOp",EDGE,"E11.25.1"),sQuery(id+"F0.wireOp",EDGE,"E11.25.2"),sQuery(id+"F0.wireOp",EDGE,"E11.25.3"),sQuery(id+"F0.wireOp",EDGE,"E11.25.4"),sQuery(id+"F0.wireOp",EDGE,"E11.25.5"),sQuery(id+"F0.wireOp",EDGE,"E11.25.6"),sQuery(id+"F0.wireOp",EDGE,"E11.25.7"),sQuery(id+"F0.wireOp",EDGE,"E11.25.8"),sQuery(id+"F0.wireOp",EDGE,"E11.25.9"),sQuery(id+"F0.wireOp",EDGE,"E11.26.0"),sQuery(id+"F0.wireOp",EDGE,"E11.26.1"),sQuery(id+"F0.wireOp",EDGE,"E11.26.2"),sQuery(id+"F0.wireOp",EDGE,"E11.26.3"),sQuery(id+"F0.wireOp",EDGE,"E11.26.4"),sQuery(id+"F0.wireOp",EDGE,"E11.26.5"),sQuery(id+"F0.wireOp",EDGE,"E11.26.6"),sQuery(id+"F0.wireOp",EDGE,"E11.26.7"),sQuery(id+"F0.wireOp",EDGE,"E11.26.8"),sQuery(id+"F0.wireOp",EDGE,"E11.26.9"),sQuery(id+"F0.wireOp",EDGE,"E11.27.0"),sQuery(id+"F0.wireOp",EDGE,"E11.27.1"),sQuery(id+"F0.wireOp",EDGE,"E11.27.2"),sQuery(id+"F0.wireOp",EDGE,"E11.27.3"),sQuery(id+"F0.wireOp",EDGE,"E11.27.4"),sQuery(id+"F0.wireOp",EDGE,"E11.27.5"),sQuery(id+"F0.wireOp",EDGE,"E11.27.6"),sQuery(id+"F0.wireOp",EDGE,"E11.27.7"),sQuery(id+"F0.wireOp",EDGE,"E11.27.8"),sQuery(id+"F0.wireOp",EDGE,"E11.27.9"),sQuery(id+"F0.wireOp",EDGE,"E11.28.0"),sQuery(id+"F0.wireOp",EDGE,"E11.28.1"),sQuery(id+"F0.wireOp",EDGE,"E11.28.2"),sQuery(id+"F0.wireOp",EDGE,"E11.28.3"),sQuery(id+"F0.wireOp",EDGE,"E11.28.4"),sQuery(id+"F0.wireOp",EDGE,"E11.28.5"),sQuery(id+"F0.wireOp",EDGE,"E11.28.6"),sQuery(id+"F0.wireOp",EDGE,"E11.28.7"),sQuery(id+"F0.wireOp",EDGE,"E11.28.8"),sQuery(id+"F0.wireOp",EDGE,"E11.28.9"),sQuery(id+"F0.wireOp",EDGE,"E11.29.0"),sQuery(id+"F0.wireOp",EDGE,"E11.29.1"),sQuery(id+"F0.wireOp",EDGE,"E11.29.2"),sQuery(id+"F0.wireOp",EDGE,"E11.29.3"),sQuery(id+"F0.wireOp",EDGE,"E11.29.4"),sQuery(id+"F0.wireOp",EDGE,"E11.29.5"),sQuery(id+"F0.wireOp",EDGE,"E11.29.6"),sQuery(id+"F0.wireOp",EDGE,"E11.29.7"),sQuery(id+"F0.wireOp",EDGE,"E11.29.8"),sQuery(id+"F0.wireOp",EDGE,"E11.29.9"),sQuery(id+"F0.wireOp",EDGE,"E11.30.0"),sQuery(id+"F0.wireOp",EDGE,"E11.30.1"),sQuery(id+"F0.wireOp",EDGE,"E11.30.2"),sQuery(id+"F0.wireOp",EDGE,"E11.30.3"),sQuery(id+"F0.wireOp",EDGE,"E11.30.4"),sQuery(id+"F0.wireOp",EDGE,"E11.30.5"),sQuery(id+"F0.wireOp",EDGE,"E11.30.6"),sQuery(id+"F0.wireOp",EDGE,"E11.30.7"),sQuery(id+"F0.wireOp",EDGE,"E11.30.8"),sQuery(id+"F0.wireOp",EDGE,"E11.30.9"),sQuery(id+"F0.wireOp",EDGE,"E11.31.0"),sQuery(id+"F0.wireOp",EDGE,"E11.31.1"),sQuery(id+"F0.wireOp",EDGE,"E11.31.2"),sQuery(id+"F0.wireOp",EDGE,"E11.31.3"),sQuery(id+"F0.wireOp",EDGE,"E11.31.4"),sQuery(id+"F0.wireOp",EDGE,"E11.31.5"),sQuery(id+"F0.wireOp",EDGE,"E11.31.6"),sQuery(id+"F0.wireOp",EDGE,"E11.31.7"),sQuery(id+"F0.wireOp",EDGE,"E11.31.8"),sQuery(id+"F0.wireOp",EDGE,"E11.31.9"),sQuery(id+"F0.wireOp",EDGE,"E11.32.0"),sQuery(id+"F0.wireOp",EDGE,"E11.32.1"),sQuery(id+"F0.wireOp",EDGE,"E11.32.2"),sQuery(id+"F0.wireOp",EDGE,"E11.32.3"),sQuery(id+"F0.wireOp",EDGE,"E11.32.4"),sQuery(id+"F0.wireOp",EDGE,"E11.32.5"),sQuery(id+"F0.wireOp",EDGE,"E11.32.6"),sQuery(id+"F0.wireOp",EDGE,"E11.32.7"),sQuery(id+"F0.wireOp",EDGE,"E11.32.8"),sQuery(id+"F0.wireOp",EDGE,"E11.32.9"),sQuery(id+"F0.wireOp",EDGE,"E11.33.0"),sQuery(id+"F0.wireOp",EDGE,"E11.33.1"),sQuery(id+"F0.wireOp",EDGE,"E11.33.2"),sQuery(id+"F0.wireOp",EDGE,"E11.33.3"),sQuery(id+"F0.wireOp",EDGE,"E11.33.4"),sQuery(id+"F0.wireOp",EDGE,"E11.33.5"),sQuery(id+"F0.wireOp",EDGE,"E11.33.6"),sQuery(id+"F0.wireOp",EDGE,"E11.33.7"),sQuery(id+"F0.wireOp",EDGE,"E11.33.8"),sQuery(id+"F0.wireOp",EDGE,"E11.33.9"),sQuery(id+"F0.wireOp",EDGE,"E11.34.0"),sQuery(id+"F0.wireOp",EDGE,"E11.34.1"),sQuery(id+"F0.wireOp",EDGE,"E11.34.2"),sQuery(id+"F0.wireOp",EDGE,"E11.34.3"),sQuery(id+"F0.wireOp",EDGE,"E11.34.4"),sQuery(id+"F0.wireOp",EDGE,"E11.34.5"),sQuery(id+"F0.wireOp",EDGE,"E11.34.6"),sQuery(id+"F0.wireOp",EDGE,"E11.34.7"),sQuery(id+"F0.wireOp",EDGE,"E11.34.8"),sQuery(id+"F0.wireOp",EDGE,"E11.34.9"),sQuery(id+"F0.wireOp",EDGE,"E11.35.0"),sQuery(id+"F0.wireOp",EDGE,"E11.35.1"),sQuery(id+"F0.wireOp",EDGE,"E11.35.2"),sQuery(id+"F0.wireOp",EDGE,"E11.35.3"),sQuery(id+"F0.wireOp",EDGE,"E11.35.4"),sQuery(id+"F0.wireOp",EDGE,"E11.35.5"),sQuery(id+"F0.wireOp",EDGE,"E11.35.6"),sQuery(id+"F0.wireOp",EDGE,"E11.35.7"),sQuery(id+"F0.wireOp",EDGE,"E11.35.8"),sQuery(id+"F0.wireOp",EDGE,"E11.35.9"),sQuery(id+"F0.wireOp",EDGE,"E11.36.0"),sQuery(id+"F0.wireOp",EDGE,"E11.36.1"),sQuery(id+"F0.wireOp",EDGE,"E11.36.2"),sQuery(id+"F0.wireOp",EDGE,"E11.36.3"),sQuery(id+"F0.wireOp",EDGE,"E11.36.4"),sQuery(id+"F0.wireOp",EDGE,"E11.36.5"),sQuery(id+"F0.wireOp",EDGE,"E11.36.6"),sQuery(id+"F0.wireOp",EDGE,"E11.36.7"),sQuery(id+"F0.wireOp",EDGE,"E11.36.8"),sQuery(id+"F0.wireOp",EDGE,"E11.36.9"),sQuery(id+"F0.wireOp",EDGE,"E11.37.0"),sQuery(id+"F0.wireOp",EDGE,"E11.37.1"),sQuery(id+"F0.wireOp",EDGE,"E11.37.2"),sQuery(id+"F0.wireOp",EDGE,"E11.37.3"),sQuery(id+"F0.wireOp",EDGE,"E11.37.4"),sQuery(id+"F0.wireOp",EDGE,"E11.37.5"),sQuery(id+"F0.wireOp",EDGE,"E11.37.6"),sQuery(id+"F0.wireOp",EDGE,"E11.37.7"),sQuery(id+"F0.wireOp",EDGE,"E11.37.8"),sQuery(id+"F0.wireOp",EDGE,"E11.37.9"),sQuery(id+"F0.wireOp",EDGE,"E11.38.0"),sQuery(id+"F0.wireOp",EDGE,"E11.38.1"),sQuery(id+"F0.wireOp",EDGE,"E11.38.2"),sQuery(id+"F0.wireOp",EDGE,"E11.38.3"),sQuery(id+"F0.wireOp",EDGE,"E11.38.4"),sQuery(id+"F0.wireOp",EDGE,"E11.38.5"),sQuery(id+"F0.wireOp",EDGE,"E11.38.6"),sQuery(id+"F0.wireOp",EDGE,"E11.38.7"),sQuery(id+"F0.wireOp",EDGE,"E11.38.8"),sQuery(id+"F0.wireOp",EDGE,"E11.38.9"),sQuery(id+"F0.wireOp",EDGE,"E11.39.0"),sQuery(id+"F0.wireOp",EDGE,"E11.39.1"),sQuery(id+"F0.wireOp",EDGE,"E11.39.2"),sQuery(id+"F0.wireOp",EDGE,"E11.39.3"),sQuery(id+"F0.wireOp",EDGE,"E11.39.4"),sQuery(id+"F0.wireOp",EDGE,"E11.39.5"),sQuery(id+"F0.wireOp",EDGE,"E11.39.6"),sQuery(id+"F0.wireOp",EDGE,"E11.39.7"),sQuery(id+"F0.wireOp",EDGE,"E11.39.8"),sQuery(id+"F0.wireOp",EDGE,"E11.39.9"),sQuery(id+"F0.wireOp",EDGE,"E11.40.0"),sQuery(id+"F0.wireOp",EDGE,"E11.40.1"),sQuery(id+"F0.wireOp",EDGE,"E11.40.2"),sQuery(id+"F0.wireOp",EDGE,"E11.40.3"),sQuery(id+"F0.wireOp",EDGE,"E11.40.4"),sQuery(id+"F0.wireOp",EDGE,"E11.40.5"),sQuery(id+"F0.wireOp",EDGE,"E11.40.6"),sQuery(id+"F0.wireOp",EDGE,"E11.40.7"),sQuery(id+"F0.wireOp",EDGE,"E11.40.8"),sQuery(id+"F0.wireOp",EDGE,"E11.40.9"),sQuery(id+"F0.wireOp",EDGE,"E11.41.0"),sQuery(id+"F0.wireOp",EDGE,"E11.41.1"),sQuery(id+"F0.wireOp",EDGE,"E11.41.2"),sQuery(id+"F0.wireOp",EDGE,"E11.41.3"),sQuery(id+"F0.wireOp",EDGE,"E11.41.4"),sQuery(id+"F0.wireOp",EDGE,"E11.41.5"),sQuery(id+"F0.wireOp",EDGE,"E11.41.6"),sQuery(id+"F0.wireOp",EDGE,"E11.41.7"),sQuery(id+"F0.wireOp",EDGE,"E11.41.8"),sQuery(id+"F0.wireOp",EDGE,"E11.41.9"),sQuery(id+"F0.wireOp",EDGE,"E11.42.0"),sQuery(id+"F0.wireOp",EDGE,"E11.42.1"),sQuery(id+"F0.wireOp",EDGE,"E11.42.2"),sQuery(id+"F0.wireOp",EDGE,"E11.42.3"),sQuery(id+"F0.wireOp",EDGE,"E11.42.4"),sQuery(id+"F0.wireOp",EDGE,"E11.42.5"),sQuery(id+"F0.wireOp",EDGE,"E11.42.6"),sQuery(id+"F0.wireOp",EDGE,"E11.42.7"),sQuery(id+"F0.wireOp",EDGE,"E11.42.8"),sQuery(id+"F0.wireOp",EDGE,"E11.42.9"),sQuery(id+"F0.wireOp",EDGE,"E11.43.0"),sQuery(id+"F0.wireOp",EDGE,"E11.43.1"),sQuery(id+"F0.wireOp",EDGE,"E11.43.2"),sQuery(id+"F0.wireOp",EDGE,"E11.43.3"),sQuery(id+"F0.wireOp",EDGE,"E11.43.4"),sQuery(id+"F0.wireOp",EDGE,"E11.43.5"),sQuery(id+"F0.wireOp",EDGE,"E11.43.6"),sQuery(id+"F0.wireOp",EDGE,"E11.43.7"),sQuery(id+"F0.wireOp",EDGE,"E11.43.8"),sQuery(id+"F0.wireOp",EDGE,"E11.43.9"),sQuery(id+"F0.wireOp",EDGE,"E11.44.0"),sQuery(id+"F0.wireOp",EDGE,"E11.44.1"),sQuery(id+"F0.wireOp",EDGE,"E11.44.2"),sQuery(id+"F0.wireOp",EDGE,"E11.44.3"),sQuery(id+"F0.wireOp",EDGE,"E11.44.4"),sQuery(id+"F0.wireOp",EDGE,"E11.44.5"),sQuery(id+"F0.wireOp",EDGE,"E11.44.6"),sQuery(id+"F0.wireOp",EDGE,"E11.44.7"),sQuery(id+"F0.wireOp",EDGE,"E11.44.8"),sQuery(id+"F0.wireOp",EDGE,"E11.44.9"),sQuery(id+"F0.wireOp",EDGE,"E11.45.0"),sQuery(id+"F0.wireOp",EDGE,"E11.45.1"),sQuery(id+"F0.wireOp",EDGE,"E11.45.2"),sQuery(id+"F0.wireOp",EDGE,"E11.45.3"),sQuery(id+"F0.wireOp",EDGE,"E11.45.4"),sQuery(id+"F0.wireOp",EDGE,"E11.45.5"),sQuery(id+"F0.wireOp",EDGE,"E11.45.6"),sQuery(id+"F0.wireOp",EDGE,"E11.45.7"),sQuery(id+"F0.wireOp",EDGE,"E11.45.8"),sQuery(id+"F0.wireOp",EDGE,"E11.45.9"),sQuery(id+"F0.wireOp",EDGE,"E11.46.0"),sQuery(id+"F0.wireOp",EDGE,"E11.46.1"),sQuery(id+"F0.wireOp",EDGE,"E11.46.2"),sQuery(id+"F0.wireOp",EDGE,"E11.46.3"),sQuery(id+"F0.wireOp",EDGE,"E11.46.4"),sQuery(id+"F0.wireOp",EDGE,"E11.46.5"),sQuery(id+"F0.wireOp",EDGE,"E11.46.6"),sQuery(id+"F0.wireOp",EDGE,"E11.46.7"),sQuery(id+"F0.wireOp",EDGE,"E11.46.8"),sQuery(id+"F0.wireOp",EDGE,"E11.46.9"),sQuery(id+"F0.wireOp",EDGE,"E11.47.0"),sQuery(id+"F0.wireOp",EDGE,"E11.47.1"),sQuery(id+"F0.wireOp",EDGE,"E11.47.2"),sQuery(id+"F0.wireOp",EDGE,"E11.47.3"),sQuery(id+"F0.wireOp",EDGE,"E11.47.4"),sQuery(id+"F0.wireOp",EDGE,"E11.47.5"),sQuery(id+"F0.wireOp",EDGE,"E11.47.6"),sQuery(id+"F0.wireOp",EDGE,"E11.47.7"),sQuery(id+"F0.wireOp",EDGE,"E11.47.8"),sQuery(id+"F0.wireOp",EDGE,"E11.47.9"),sQuery(id+"F0.wireOp",EDGE,"E11.48.0"),sQuery(id+"F0.wireOp",EDGE,"E11.48.1"),sQuery(id+"F0.wireOp",EDGE,"E11.48.2"),sQuery(id+"F0.wireOp",EDGE,"E11.48.3"),sQuery(id+"F0.wireOp",EDGE,"E11.48.4"),sQuery(id+"F0.wireOp",EDGE,"E11.48.5"),sQuery(id+"F0.wireOp",EDGE,"E11.48.6"),sQuery(id+"F0.wireOp",EDGE,"E11.48.7"),sQuery(id+"F0.wireOp",EDGE,"E11.48.8"),sQuery(id+"F0.wireOp",EDGE,"E11.48.9"),sQuery(id+"F0.wireOp",EDGE,"E11.49.0"),sQuery(id+"F0.wireOp",EDGE,"E11.49.1"),sQuery(id+"F0.wireOp",EDGE,"E11.49.2"),sQuery(id+"F0.wireOp",EDGE,"E11.49.3"),sQuery(id+"F0.wireOp",EDGE,"E11.49.4"),sQuery(id+"F0.wireOp",EDGE,"E11.49.5"),sQuery(id+"F0.wireOp",EDGE,"E11.49.6"),sQuery(id+"F0.wireOp",EDGE,"E11.49.7"),sQuery(id+"F0.wireOp",EDGE,"E11.49.8"),sQuery(id+"F0.wireOp",EDGE,"E11.49.9"),sQuery(id+"F0.wireOp",EDGE,"E11.50.0"),sQuery(id+"F0.wireOp",EDGE,"E11.50.1"),sQuery(id+"F0.wireOp",EDGE,"E11.50.2"),sQuery(id+"F0.wireOp",EDGE,"E11.50.3"),sQuery(id+"F0.wireOp",EDGE,"E11.50.4"),sQuery(id+"F0.wireOp",EDGE,"E11.50.5"),sQuery(id+"F0.wireOp",EDGE,"E11.50.6"),sQuery(id+"F0.wireOp",EDGE,"E11.50.7"),sQuery(id+"F0.wireOp",EDGE,"E11.50.8"),sQuery(id+"F0.wireOp",EDGE,"E11.50.9"),sQuery(id+"F0.wireOp",EDGE,"E11.51.0"),sQuery(id+"F0.wireOp",EDGE,"E11.51.1"),sQuery(id+"F0.wireOp",EDGE,"E11.51.2"),sQuery(id+"F0.wireOp",EDGE,"E11.51.3"),sQuery(id+"F0.wireOp",EDGE,"E11.51.4"),sQuery(id+"F0.wireOp",EDGE,"E11.51.5"),sQuery(id+"F0.wireOp",EDGE,"E11.51.6"),sQuery(id+"F0.wireOp",EDGE,"E11.51.7"),sQuery(id+"F0.wireOp",EDGE,"E11.51.8"),sQuery(id+"F0.wireOp",EDGE,"E11.51.9"),sQuery(id+"F0.wireOp",EDGE,"E11.52.0"),sQuery(id+"F0.wireOp",EDGE,"E11.52.1"),sQuery(id+"F0.wireOp",EDGE,"E11.52.2"),sQuery(id+"F0.wireOp",EDGE,"E11.52.3"),sQuery(id+"F0.wireOp",EDGE,"E11.52.4"),sQuery(id+"F0.wireOp",EDGE,"E11.52.5"),sQuery(id+"F0.wireOp",EDGE,"E11.52.6"),sQuery(id+"F0.wireOp",EDGE,"E11.52.7"),sQuery(id+"F0.wireOp",EDGE,"E11.52.8"),sQuery(id+"F0.wireOp",EDGE,"E11.52.9"),sQuery(id+"F0.wireOp",EDGE,"E11.53.0"),sQuery(id+"F0.wireOp",EDGE,"E11.53.1"),sQuery(id+"F0.wireOp",EDGE,"E11.53.2"),sQuery(id+"F0.wireOp",EDGE,"E11.53.3"),sQuery(id+"F0.wireOp",EDGE,"E11.53.4"),sQuery(id+"F0.wireOp",EDGE,"E11.53.5"),sQuery(id+"F0.wireOp",EDGE,"E11.53.6"),sQuery(id+"F0.wireOp",EDGE,"E11.53.7"),sQuery(id+"F0.wireOp",EDGE,"E11.53.8"),sQuery(id+"F0.wireOp",EDGE,"E11.53.9"),sQuery(id+"F0.wireOp",EDGE,"E11.54.0"),sQuery(id+"F0.wireOp",EDGE,"E11.54.1"),sQuery(id+"F0.wireOp",EDGE,"E11.54.2"),sQuery(id+"F0.wireOp",EDGE,"E11.54.3"),sQuery(id+"F0.wireOp",EDGE,"E11.54.4"),sQuery(id+"F0.wireOp",EDGE,"E11.54.5"),sQuery(id+"F0.wireOp",EDGE,"E11.54.6"),sQuery(id+"F0.wireOp",EDGE,"E11.54.7"),sQuery(id+"F0.wireOp",EDGE,"E11.54.8"),sQuery(id+"F0.wireOp",EDGE,"E11.54.9"),sQuery(id+"F0.wireOp",EDGE,"E11.55.0"),sQuery(id+"F0.wireOp",EDGE,"E11.55.1"),sQuery(id+"F0.wireOp",EDGE,"E11.55.2"),sQuery(id+"F0.wireOp",EDGE,"E11.55.3"),sQuery(id+"F0.wireOp",EDGE,"E11.55.4"),sQuery(id+"F0.wireOp",EDGE,"E11.55.5"),sQuery(id+"F0.wireOp",EDGE,"E11.55.6"),sQuery(id+"F0.wireOp",EDGE,"E11.55.7"),sQuery(id+"F0.wireOp",EDGE,"E11.55.8"),sQuery(id+"F0.wireOp",EDGE,"E11.55.9"),sQuery(id+"F0.wireOp",EDGE,"E11.56.0"),sQuery(id+"F0.wireOp",EDGE,"E11.56.1"),sQuery(id+"F0.wireOp",EDGE,"E11.56.2"),sQuery(id+"F0.wireOp",EDGE,"E11.56.3"),sQuery(id+"F0.wireOp",EDGE,"E11.56.4"),sQuery(id+"F0.wireOp",EDGE,"E11.56.5"),sQuery(id+"F0.wireOp",EDGE,"E11.56.6"),sQuery(id+"F0.wireOp",EDGE,"E11.56.7"),sQuery(id+"F0.wireOp",EDGE,"E11.56.8"),sQuery(id+"F0.wireOp",EDGE,"E11.56.9"),sQuery(id+"F0.wireOp",EDGE,"E11.57.0"),sQuery(id+"F0.wireOp",EDGE,"E11.57.1"),sQuery(id+"F0.wireOp",EDGE,"E11.57.2"),sQuery(id+"F0.wireOp",EDGE,"E11.57.3"),sQuery(id+"F0.wireOp",EDGE,"E11.57.4"),sQuery(id+"F0.wireOp",EDGE,"E11.57.5"),sQuery(id+"F0.wireOp",EDGE,"E11.57.6"),sQuery(id+"F0.wireOp",EDGE,"E11.57.7"),sQuery(id+"F0.wireOp",EDGE,"E11.57.8"),sQuery(id+"F0.wireOp",EDGE,"E11.57.9"),sQuery(id+"F0.wireOp",EDGE,"E11.58.0"),sQuery(id+"F0.wireOp",EDGE,"E11.58.1"),sQuery(id+"F0.wireOp",EDGE,"E11.58.2"),sQuery(id+"F0.wireOp",EDGE,"E11.58.3"),sQuery(id+"F0.wireOp",EDGE,"E11.58.4"),sQuery(id+"F0.wireOp",EDGE,"E11.58.5"),sQuery(id+"F0.wireOp",EDGE,"E11.58.6"),sQuery(id+"F0.wireOp",EDGE,"E11.58.7"),sQuery(id+"F0.wireOp",EDGE,"E11.58.8"),sQuery(id+"F0.wireOp",EDGE,"E11.58.9"),sQuery(id+"F0.wireOp",EDGE,"E11.59.0"),sQuery(id+"F0.wireOp",EDGE,"E11.59.1"),sQuery(id+"F0.wireOp",EDGE,"E11.59.2"),sQuery(id+"F0.wireOp",EDGE,"E11.59.3"),sQuery(id+"F0.wireOp",EDGE,"E11.59.4"),sQuery(id+"F0.wireOp",EDGE,"E11.59.5"),sQuery(id+"F0.wireOp",EDGE,"E11.59.6"),sQuery(id+"F0.wireOp",EDGE,"E11.59.7"),sQuery(id+"F0.wireOp",EDGE,"E11.59.8"),sQuery(id+"F0.wireOp",EDGE,"E11.59.9"),sQuery(id+"F0.wireOp",EDGE,"E11.60.0"),sQuery(id+"F0.wireOp",EDGE,"E11.60.1"),sQuery(id+"F0.wireOp",EDGE,"E11.60.2"),sQuery(id+"F0.wireOp",EDGE,"E11.60.3"),sQuery(id+"F0.wireOp",EDGE,"E11.60.4"),sQuery(id+"F0.wireOp",EDGE,"E11.60.5"),sQuery(id+"F0.wireOp",EDGE,"E11.60.6"),sQuery(id+"F0.wireOp",EDGE,"E11.60.7"),sQuery(id+"F0.wireOp",EDGE,"E11.60.8"),sQuery(id+"F0.wireOp",EDGE,"E11.60.9"),sQuery(id+"F0.wireOp",EDGE,"E11.61.0"),sQuery(id+"F0.wireOp",EDGE,"E11.61.1"),sQuery(id+"F0.wireOp",EDGE,"E11.61.2"),sQuery(id+"F0.wireOp",EDGE,"E11.61.3"),sQuery(id+"F0.wireOp",EDGE,"E11.61.4"),sQuery(id+"F0.wireOp",EDGE,"E11.61.5"),sQuery(id+"F0.wireOp",EDGE,"E11.61.6"),sQuery(id+"F0.wireOp",EDGE,"E11.61.7"),sQuery(id+"F0.wireOp",EDGE,"E11.61.8"),sQuery(id+"F0.wireOp",EDGE,"E11.61.9"),sQuery(id+"F0.wireOp",EDGE,"E11.62.0"),sQuery(id+"F0.wireOp",EDGE,"E11.62.1"),sQuery(id+"F0.wireOp",EDGE,"E11.62.2"),sQuery(id+"F0.wireOp",EDGE,"E11.62.3"),sQuery(id+"F0.wireOp",EDGE,"E11.62.4"),sQuery(id+"F0.wireOp",EDGE,"E11.62.5"),sQuery(id+"F0.wireOp",EDGE,"E11.62.6"),sQuery(id+"F0.wireOp",EDGE,"E11.62.7"),sQuery(id+"F0.wireOp",EDGE,"E11.62.8"),sQuery(id+"F0.wireOp",EDGE,"E11.62.9"),sQuery(id+"F0.wireOp",EDGE,"E11.63.0"),sQuery(id+"F0.wireOp",EDGE,"E11.63.1"),sQuery(id+"F0.wireOp",EDGE,"E11.63.2"),sQuery(id+"F0.wireOp",EDGE,"E11.63.3"),sQuery(id+"F0.wireOp",EDGE,"E11.63.4"),sQuery(id+"F0.wireOp",EDGE,"E11.63.5"),sQuery(id+"F0.wireOp",EDGE,"E11.63.6"),sQuery(id+"F0.wireOp",EDGE,"E11.63.7"),sQuery(id+"F0.wireOp",EDGE,"E11.63.8"),sQuery(id+"F0.wireOp",EDGE,"E11.63.9"),sQuery(id+"F0.wireOp",EDGE,"E11.64.0"),sQuery(id+"F0.wireOp",EDGE,"E11.64.1"),sQuery(id+"F0.wireOp",EDGE,"E11.64.2"),sQuery(id+"F0.wireOp",EDGE,"E11.64.3"),sQuery(id+"F0.wireOp",EDGE,"E11.64.4"),sQuery(id+"F0.wireOp",EDGE,"E11.64.5"),sQuery(id+"F0.wireOp",EDGE,"E11.64.6"),sQuery(id+"F0.wireOp",EDGE,"E11.64.7"),sQuery(id+"F0.wireOp",EDGE,"E11.64.8"),sQuery(id+"F0.wireOp",EDGE,"E11.64.9"),sQuery(id+"F0.wireOp",EDGE,"E11.65.0"),sQuery(id+"F0.wireOp",EDGE,"E11.65.1"),sQuery(id+"F0.wireOp",EDGE,"E11.65.2"),sQuery(id+"F0.wireOp",EDGE,"E11.65.3"),sQuery(id+"F0.wireOp",EDGE,"E11.65.4"),sQuery(id+"F0.wireOp",EDGE,"E11.65.5"),sQuery(id+"F0.wireOp",EDGE,"E11.65.6"),sQuery(id+"F0.wireOp",EDGE,"E11.65.7"),sQuery(id+"F0.wireOp",EDGE,"E11.65.8"),sQuery(id+"F0.wireOp",EDGE,"E11.65.9"),sQuery(id+"F0.wireOp",EDGE,"E11.66.0"),sQuery(id+"F0.wireOp",EDGE,"E11.66.1"),sQuery(id+"F0.wireOp",EDGE,"E11.66.2"),sQuery(id+"F0.wireOp",EDGE,"E11.66.3"),sQuery(id+"F0.wireOp",EDGE,"E11.66.4"),sQuery(id+"F0.wireOp",EDGE,"E11.66.5"),sQuery(id+"F0.wireOp",EDGE,"E11.66.6"),sQuery(id+"F0.wireOp",EDGE,"E11.66.7"),sQuery(id+"F0.wireOp",EDGE,"E11.66.8"),sQuery(id+"F0.wireOp",EDGE,"E11.66.9"),sQuery(id+"F0.wireOp",EDGE,"E11.67.0"),sQuery(id+"F0.wireOp",EDGE,"E11.67.1"),sQuery(id+"F0.wireOp",EDGE,"E11.67.2"),sQuery(id+"F0.wireOp",EDGE,"E11.67.3"),sQuery(id+"F0.wireOp",EDGE,"E11.67.4"),sQuery(id+"F0.wireOp",EDGE,"E11.67.5"),sQuery(id+"F0.wireOp",EDGE,"E11.67.6"),sQuery(id+"F0.wireOp",EDGE,"E11.67.7"),sQuery(id+"F0.wireOp",EDGE,"E11.67.8"),sQuery(id+"F0.wireOp",EDGE,"E11.67.9"),sQuery(id+"F0.wireOp",EDGE,"E11.68.0"),sQuery(id+"F0.wireOp",EDGE,"E11.68.1"),sQuery(id+"F0.wireOp",EDGE,"E11.68.2"),sQuery(id+"F0.wireOp",EDGE,"E11.68.3"),sQuery(id+"F0.wireOp",EDGE,"E11.68.4"),sQuery(id+"F0.wireOp",EDGE,"E11.68.5"),sQuery(id+"F0.wireOp",EDGE,"E11.68.6"),sQuery(id+"F0.wireOp",EDGE,"E11.68.7"),sQuery(id+"F0.wireOp",EDGE,"E11.68.8"),sQuery(id+"F0.wireOp",EDGE,"E11.68.9"),sQuery(id+"F0.wireOp",EDGE,"E11.69.0"),sQuery(id+"F0.wireOp",EDGE,"E11.69.1"),sQuery(id+"F0.wireOp",EDGE,"E11.69.2"),sQuery(id+"F0.wireOp",EDGE,"E11.69.3"),sQuery(id+"F0.wireOp",EDGE,"E11.69.4"),sQuery(id+"F0.wireOp",EDGE,"E11.69.5"),sQuery(id+"F0.wireOp",EDGE,"E11.69.6"),sQuery(id+"F0.wireOp",EDGE,"E11.69.7"),sQuery(id+"F0.wireOp",EDGE,"E11.69.8"),sQuery(id+"F0.wireOp",EDGE,"E11.69.9"),sQuery(id+"F0.wireOp",EDGE,"E11.70.0"),sQuery(id+"F0.wireOp",EDGE,"E11.70.1"),sQuery(id+"F0.wireOp",EDGE,"E11.70.2"),sQuery(id+"F0.wireOp",EDGE,"E11.70.3"),sQuery(id+"F0.wireOp",EDGE,"E11.70.4"),sQuery(id+"F0.wireOp",EDGE,"E11.70.5"),sQuery(id+"F0.wireOp",EDGE,"E11.70.6"),sQuery(id+"F0.wireOp",EDGE,"E11.70.7"),sQuery(id+"F0.wireOp",EDGE,"E11.70.8"),sQuery(id+"F0.wireOp",EDGE,"E11.70.9"),sQuery(id+"F0.wireOp",EDGE,"E11.71.0"),sQuery(id+"F0.wireOp",EDGE,"E11.71.1"),sQuery(id+"F0.wireOp",EDGE,"E11.71.2"),sQuery(id+"F0.wireOp",EDGE,"E11.71.3"),sQuery(id+"F0.wireOp",EDGE,"E11.71.4"),sQuery(id+"F0.wireOp",EDGE,"E11.71.5"),sQuery(id+"F0.wireOp",EDGE,"E11.71.6"),sQuery(id+"F0.wireOp",EDGE,"E11.71.7"),sQuery(id+"F0.wireOp",EDGE,"E11.71.8"),sQuery(id+"F0.wireOp",EDGE,"E11.71.9"),sQuery(id+"F0.wireOp",EDGE,"E12.trimOffspring"),sQuery(id+"F0.wireOp",EDGE,"E13.trimOffspring"),sQuery(id+"F0.wireOp",EDGE,"E14.trimOffspring"),sQuery(id+"F0.wireOp",EDGE,"E15.trimOffspring"),sQuery(id+"F0.wireOp",EDGE,"E16.trimOffspring"),sQuery(id+"F0.wireOp",EDGE,"E17.trimOffspring"),sQuery(id+"F0.wireOp",EDGE,"E18.trimOffspring"),sQuery(id+"F0.wireOp",EDGE,"E19.trimOffspring"),sQuery(id+"F0.wireOp",EDGE,"E20.trimOffspring"),sQuery(id+"F0.wireOp",EDGE,"E21.trimOffspring"),sQuery(id+"F0.wireOp",EDGE,"E22.trimOffspring"),sQuery(id+"F0.wireOp",EDGE,"E23.trimOffspring"),sQuery(id+"F0.wireOp",EDGE,"E24.trimOffspring"),sQuery(id+"F0.wireOp",EDGE,"E25.trimOffspring"),sQuery(id+"F0.wireOp",EDGE,"E26.trimOffspring"),sQuery(id+"F0.wireOp",EDGE,"E27.trimOffspring"),sQuery(id+"F0.wireOp",EDGE,"E28.trimOffspring"),sQuery(id+"F0.wireOp",EDGE,"E29.trimOffspring"),sQuery(id+"F0.wireOp",EDGE,"E30.trimOffspring"),sQuery(id+"F0.wireOp",EDGE,"E31.trimOffspring"),sQuery(id+"F0.wireOp",EDGE,"E32.trimOffspring"),sQuery(id+"F0.wireOp",EDGE,"E33.trimOffspring"),sQuery(id+"F0.wireOp",EDGE,"E34.trimOffspring"),sQuery(id+"F0.wireOp",EDGE,"E35.trimOffspring"),sQuery(id+"F0.wireOp",EDGE,"E36.trimOffspring"),sQuery(id+"F0.wireOp",EDGE,"E37.trimOffspring"),sQuery(id+"F0.wireOp",EDGE,"E38.trimOffspring"),sQuery(id+"F0.wireOp",EDGE,"E39.trimOffspring"),sQuery(id+"F0.wireOp",EDGE,"E40.trimOffspring"),sQuery(id+"F0.wireOp",EDGE,"E41.trimOffspring"),sQuery(id+"F0.wireOp",EDGE,"E42.trimOffspring"),sQuery(id+"F0.wireOp",EDGE,"E43.trimOffspring"),sQuery(id+"F0.wireOp",EDGE,"E44.trimOffspring"),sQuery(id+"F0.wireOp",EDGE,"E45.trimOffspring"),sQuery(id+"F0.wireOp",EDGE,"E46.trimOffspring"),sQuery(id+"F0.wireOp",EDGE,"E47.trimOffspring"),sQuery(id+"F0.wireOp",EDGE,"E48.trimOffspring"),sQuery(id+"F0.wireOp",EDGE,"E49.trimOffspring"),sQuery(id+"F0.wireOp",EDGE,"E50.trimOffspring"),sQuery(id+"F0.wireOp",EDGE,"E51.trimOffspring"),sQuery(id+"F0.wireOp",EDGE,"E52.trimOffspring"),sQuery(id+"F0.wireOp",EDGE,"E53.trimOffspring"),sQuery(id+"F0.wireOp",EDGE,"E54.trimOffspring"),sQuery(id+"F0.wireOp",EDGE,"E55.trimOffspring"),sQuery(id+"F0.wireOp",EDGE,"E56.trimOffspring"),sQuery(id+"F0.wireOp",EDGE,"E57.trimOffspring"),sQuery(id+"F0.wireOp",EDGE,"E58.trimOffspring"),sQuery(id+"F0.wireOp",EDGE,"E59.trimOffspring"),sQuery(id+"F0.wireOp",EDGE,"E60.trimOffspring"),sQuery(id+"F0.wireOp",EDGE,"E61.trimOffspring"),sQuery(id+"F0.wireOp",EDGE,"E62.trimOffspring"),sQuery(id+"F0.wireOp",EDGE,"E63.trimOffspring"),sQuery(id+"F0.wireOp",EDGE,"E64.trimOffspring"),sQuery(id+"F0.wireOp",EDGE,"E65.trimOffspring"),sQuery(id+"F0.wireOp",EDGE,"E66.trimOffspring"),sQuery(id+"F0.wireOp",EDGE,"E67.trimOffspring"),sQuery(id+"F0.wireOp",EDGE,"E68.trimOffspring"),sQuery(id+"F0.wireOp",EDGE,"E69.trimOffspring"),sQuery(id+"F0.wireOp",EDGE,"E70.trimOffspring"),sQuery(id+"F0.wireOp",EDGE,"E71.trimOffspring"),sQuery(id+"F0.wireOp",EDGE,"E72.trimOffspring"),sQuery(id+"F0.wireOp",EDGE,"E73.trimOffspring"),sQuery(id+"F0.wireOp",EDGE,"E74.trimOffspring"),sQuery(id+"F0.wireOp",EDGE,"E75.trimOffspring"),sQuery(id+"F0.wireOp",EDGE,"E76.trimOffspring"),sQuery(id+"F0.wireOp",EDGE,"E77.trimOffspring"),sQuery(id+"F0.wireOp",EDGE,"E78.trimOffspring"),sQuery(id+"F0.wireOp",EDGE,"E79.trimOffspring"),sQuery(id+"F0.wireOp",EDGE,"E80.trimOffspring"),sQuery(id+"F0.wireOp",EDGE,"E81.trimOffspring"),sQuery(id+"F0.wireOp",EDGE,"E82"),sQuery(id+"F0.wireOp",EDGE,"E83")])],"isStart":true});
            var sketch = newSketch(context, id + "F2", { "sketchPlane" : qUnion([Q0])});
            skCircle(sketch, "E84", {"center": v(0, 0) * mm, "radius": 82.55 * mm});
            skSolve(sketch);
        }
        {
            var Q0;
            Q0 = qSketchRegion(id + "F2", true);
            extrude(context, id + "F3", {"entities" : qUnion([Q0]), "operationType" : NewBodyOperationType.ADD, "oppositeDirection" : true, "depth" : 2.54 * mm});
        }
        {
            var Q0;
            Q0=makeQuery(id+"F3.opExtrude","CAP_FACE",FACE,{"disambiguationData":[OSD([sQuery(id+"F2.wireOp",EDGE,"E84")])],"isStart":false});
            var sketch = newSketch(context, id + "F4", { "sketchPlane" : qUnion([Q0])});
            skCircle(sketch, "E85", {"center": v(0, 50.8) * mm, "radius": 5.08 * mm});
            skCircle(sketch, "E86.1.0", {"center": v(-44, -25.4) * mm, "radius": 5.08 * mm});
            skCircle(sketch, "E86.2.0", {"center": v(44, -25.4) * mm, "radius": 5.08 * mm});
            skPoint(sketch, "E86.center", {"position": v(0, 0) * mm});
            skSolve(sketch);
        }
        {
            var Q0;
            Q0 = qSketchRegion(id + "F4", true);
            extrude(context, id + "F5", {"entities" : qUnion([Q0]), "operationType" : NewBodyOperationType.ADD, "depth" : 2.54 * mm});
        }
    });
